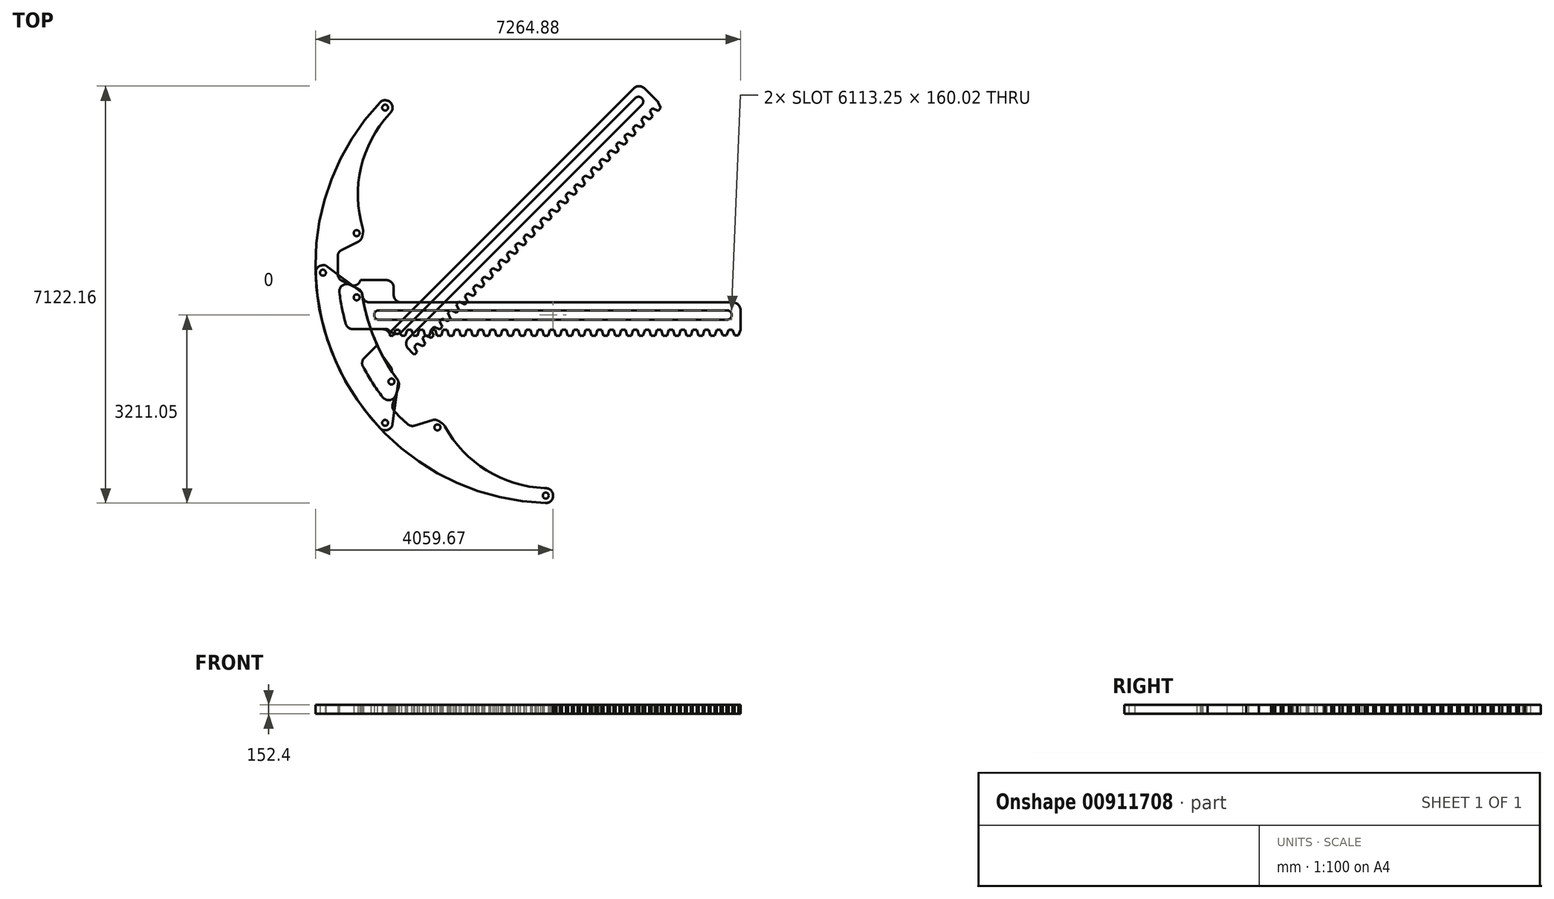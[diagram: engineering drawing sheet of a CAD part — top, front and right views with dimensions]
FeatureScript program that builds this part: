
annotation { "Feature Type Name" : "Feature", "Feature Type Description" : "" }
export const myFeature = defineFeature(function(context is Context, id is Id, definition is map)
    precondition{}
    {
        {
            var Q0;
            Q0=qCreatedBy(makeId("Top.planeOp"),FACE);
            var sketch = newSketch(context, id + "F0", { "sketchPlane" : qUnion([Q0])});
            skPoint(sketch, "E0.middle", {"position": v(0, 0) * mm});
            skCircle(sketch, "E1", {"center": v(0, 0) * mm, "radius": 3302 * mm});
            skCircle(sketch, "E2", {"center": v(0, 0) * mm, "radius": 3810 * mm});
            skCircle(sketch, "E3", {"center": v(0, 0) * mm, "radius": 3492.5 * mm, "construction": true});
            skCircle(sketch, "E4", {"center": v(0, 0) * mm, "radius": 4064 * mm});
            skLineSegment(sketch, "E5", {"start": v(0, 0) * mm, "end": v(-4064, 0) * mm});
            skCircle(sketch, "E6", {"center": v(0, 0) * mm, "radius": 3683 * mm});
            skLineSegment(sketch, "E7", {"start": v(-2740.49, -1842) * mm, "end": v(-3338.4, -1836.09) * mm});
            skLineSegment(sketch, "E8", {"start": v(-2604.27, -2604.27) * mm, "end": v(-2765.92, -2442.63) * mm});
            skLineSegment(sketch, "E9", {"start": v(-2765.92, -2442.63) * mm, "end": v(-2620.35, -2009.22) * mm});
            skLineSegment(sketch, "E10", {"start": v(0, 0) * mm, "end": v(-2873.68, -2873.68) * mm});
            skLineSegment(sketch, "E11.0", {"start": v(-2620.35, -2009.22) * mm, "end": v(-2596.8, -1985.68) * mm, "construction": true});
            skLineSegment(sketch, "E11.1", {"start": v(-2596.8, -1985.68) * mm, "end": v(-2740.49, -1842) * mm, "construction": true});
            skLineSegment(sketch, "E12", {"start": v(-2604.27, -2604.27) * mm, "end": v(-2437.7, -2760.82) * mm});
            skLineSegment(sketch, "E13", {"start": v(-2437.7, -2760.82) * mm, "end": v(-2000.51, -2627) * mm});
            skLineSegment(sketch, "E14", {"start": v(-2000.51, -2627) * mm, "end": v(-1835.14, -2745.08) * mm});
            skLineSegment(sketch, "E15", {"start": v(-1835.14, -2745.08) * mm, "end": v(-1845.2, -3333.36) * mm});
            skLineSegment(sketch, "E16", {"start": v(0, 0) * mm, "end": v(0, -4064) * mm});
            skCircle(sketch, "E17", {"center": v(-2763.42, -1986.96) * mm, "radius": 50.8 * mm});
            skCircle(sketch, "E18", {"center": v(-1977.77, -2770) * mm, "radius": 50.8 * mm});
            skLineSegment(sketch, "E19", {"start": v(0, 0) * mm, "end": v(-3299.6, -2372.49) * mm, "construction": true});
            skLineSegment(sketch, "E20", {"start": v(0, 0) * mm, "end": v(-2361.52, -3307.46) * mm, "construction": true});
            skCircle(sketch, "E21", {"center": v(-127, -3934.95) * mm, "radius": 50.8 * mm});
            skCircle(sketch, "E22", {"center": v(-3934.95, -127) * mm, "radius": 50.8 * mm});
            skSolve(sketch);
        }
        {
            var Q0;
            {var subQ0=sQuery(id+"F0.wireOp",EDGE,"E2");var subQ8=makeQuery(id+"F0.imprint","INTERSECT",VERTEX,{"derivedFrom":[subQ0,sQuery(id+"F0.wireOp",EDGE,"E7")]});Q0=makeQuery(id+"F0.imprint","IMPRINT",FACE,{"disambiguationData":[TD([[makeQuery(id+"F0.imprint","IMPRINT",EDGE,{"disambiguationData":[TD([[subQ8,1.0]])],"derivedFrom":subQ0}),-1.0]])]});}
            var Q1;
            {var subQ3=sQuery(id+"F0.wireOp",EDGE,"E7");Q1=makeQuery(id+"F0.imprint","IMPRINT",FACE,{"disambiguationData":[TD([[makeQuery(id+"F0.imprint","IMPRINT",EDGE,{"derivedFrom":subQ3}),1.0]])]});}
            var Q2;
            {var subQ0=sQuery(id+"F0.wireOp",EDGE,"E7");var subQ1=sQuery(id+"F0.wireOp",EDGE,"E1");var subQ2=makeQuery(id+"F0.imprint","INTERSECT",VERTEX,{"derivedFrom":[subQ1,subQ0]});Q2=makeQuery(id+"F0.imprint","IMPRINT",FACE,{"disambiguationData":[TD([[makeQuery(id+"F0.imprint","IMPRINT",EDGE,{"disambiguationData":[TD([[subQ2,-1.0]])],"derivedFrom":subQ1}),-1.0]])]});}
            var Q3;
            {var subQ0=sQuery(id+"F0.wireOp",EDGE,"E9");var subQ1=sQuery(id+"F0.wireOp",EDGE,"S5sV3fft-Mi81-JVDm-EhU3-nDH7DOH9WXkB");var subQ2=makeQuery(id+"F0.imprint","INTERSECT",VERTEX,{"derivedFrom":[subQ1,subQ0]});Q3=makeQuery(id+"F0.imprint","IMPRINT",FACE,{"disambiguationData":[TD([[makeQuery(id+"F0.imprint","IMPRINT",EDGE,{"disambiguationData":[TD([[subQ2,-1.0]])],"derivedFrom":subQ1}),1.0]])]});}
            var Q4;
            {var subQ9=sQuery(id+"F0.wireOp",EDGE,"E8");Q4=makeQuery(id+"F0.imprint","IMPRINT",FACE,{"disambiguationData":[TD([[makeQuery(id+"F0.imprint","IMPRINT",EDGE,{"derivedFrom":subQ9}),1.0]])]});}
            var Q5;
            {var subQ5=sQuery(id+"F0.wireOp",EDGE,"E2");var subQ6=makeQuery(id+"F0.imprint","INTERSECT",VERTEX,{"derivedFrom":[subQ5,sQuery(id+"F0.wireOp",EDGE,"E15")]});Q5=makeQuery(id+"F0.imprint","IMPRINT",FACE,{"disambiguationData":[TD([[makeQuery(id+"F0.imprint","IMPRINT",EDGE,{"disambiguationData":[TD([[subQ6,1.0]])],"derivedFrom":subQ5}),-1.0]])]});}
            var Q6;
            {var subQ4=sQuery(id+"F0.wireOp",EDGE,"E2");var subQ7=sQuery(id+"F0.wireOp",EDGE,"E15");var subQ9=makeQuery(id+"F0.imprint","INTERSECT",VERTEX,{"derivedFrom":[subQ4,subQ7]});Q6=makeQuery(id+"F0.imprint","IMPRINT",FACE,{"disambiguationData":[TD([[makeQuery(id+"F0.imprint","IMPRINT",EDGE,{"disambiguationData":[TD([[subQ9,1.0]])],"derivedFrom":subQ4}),1.0]])]});}
            var Q7;
            {var subQ1=sQuery(id+"F0.wireOp",EDGE,"E13");Q7=makeQuery(id+"F0.imprint","IMPRINT",FACE,{"disambiguationData":[TD([[makeQuery(id+"F0.imprint","IMPRINT",EDGE,{"derivedFrom":subQ1}),-1.0]])]});}
            var Q8;
            {var subQ0=sQuery(id+"F0.wireOp",EDGE,"E7");var subQ1=sQuery(id+"F0.wireOp",EDGE,"E1");var subQ2=makeQuery(id+"F0.imprint","INTERSECT",VERTEX,{"derivedFrom":[subQ1,subQ0]});Q8=makeQuery(id+"F0.imprint","IMPRINT",FACE,{"disambiguationData":[TD([[makeQuery(id+"F0.imprint","IMPRINT",EDGE,{"disambiguationData":[TD([[subQ2,1.0]])],"derivedFrom":subQ1}),-1.0]])]});}
            var Q9;
            {var subQ0=sQuery(id+"F0.wireOp",EDGE,"E7");var subQ1=sQuery(id+"F0.wireOp",EDGE,"E2");var subQ2=makeQuery(id+"F0.imprint","INTERSECT",VERTEX,{"derivedFrom":[subQ1,subQ0]});Q9=makeQuery(id+"F0.imprint","IMPRINT",FACE,{"disambiguationData":[TD([[makeQuery(id+"F0.imprint","IMPRINT",EDGE,{"disambiguationData":[TD([[subQ2,1.0]])],"derivedFrom":subQ1}),1.0]])]});}
            extrude(context, id + "F1", {"entities" : qUnion([Q0, Q1, Q2, Q3, Q4, Q5, Q6, Q7, Q8, Q9]), "depth" : 152.4 * mm, "offsetDistance" : 25.4 * mm});
        }
        {
            var Q0;
            Q0=makeQuery(id+"F1.opExtrude","SWEPT_EDGE",EDGE,{"disambiguationData":[OSD([sQuery(id+"F0.wireOp",EDGE,"E4"),sQuery(id+"F0.wireOp",EDGE,"E5")])]});
            var Q1;
            Q1=makeQuery(id+"F1.opExtrude","SWEPT_EDGE",EDGE,{"disambiguationData":[OSD([sQuery(id+"F0.wireOp",EDGE,"E2"),sQuery(id+"F0.wireOp",EDGE,"E16")])]});
            var Q2;
            Q2=makeQuery(id+"F1.opExtrude","SWEPT_EDGE",EDGE,{"disambiguationData":[OSD([sQuery(id+"F0.wireOp",EDGE,"E1"),sQuery(id+"F0.wireOp",EDGE,"E9")])]});
            var Q3;
            Q3=makeQuery(id+"F1.opExtrude","SWEPT_EDGE",EDGE,{"disambiguationData":[OSD([sQuery(id+"F0.wireOp",EDGE,"E8"),sQuery(id+"F0.wireOp",EDGE,"E9")])]});
            var Q4;
            Q4=makeQuery(id+"F1.opExtrude","SWEPT_EDGE",EDGE,{"disambiguationData":[OSD([sQuery(id+"F0.wireOp",EDGE,"E4"),sQuery(id+"F0.wireOp",EDGE,"E16")])]});
            var Q5;
            Q5=makeQuery(id+"F1.opExtrude","SWEPT_EDGE",EDGE,{"disambiguationData":[OSD([sQuery(id+"F0.wireOp",EDGE,"E6"),sQuery(id+"F0.wireOp",EDGE,"E12"),sQuery(id+"F0.wireOp",EDGE,"E13")])]});
            var Q6;
            Q6=makeQuery(id+"F1.opExtrude","SWEPT_EDGE",EDGE,{"disambiguationData":[OSD([sQuery(id+"F0.wireOp",EDGE,"E1"),sQuery(id+"F0.wireOp",EDGE,"E13"),sQuery(id+"F0.wireOp",EDGE,"E14")])]});
            var Q7;
            Q7=makeQuery(id+"F1.opExtrude","SWEPT_EDGE",EDGE,{"disambiguationData":[OSD([sQuery(id+"F0.wireOp",EDGE,"E1"),sQuery(id+"F0.wireOp",EDGE,"E14"),sQuery(id+"F0.wireOp",EDGE,"E15")])]});
            fillet(context, id + "F2", {"entities" : qUnion([Q0, Q1, Q2, Q3, Q4, Q5, Q6, Q7]), "tangentPropagation" : true, "radius" : 127 * mm, "defaultsChanged" : false, "vertexSettings" : [], "allowEdgeOverflow" : false});
        }
        {
            var Q0;
            Q0=makeQuery(id+"F1.opExtrude","SWEPT_EDGE",EDGE,{"disambiguationData":[OSD([sQuery(id+"F0.wireOp",EDGE,"E2"),sQuery(id+"F0.wireOp",EDGE,"E7")])]});
            fillet(context, id + "F3", {"entities" : qUnion([Q0]), "tangentPropagation" : true, "radius" : 2032 * mm, "defaultsChanged" : true, "vertexSettings" : [], "allowEdgeOverflow" : false});
        }
        {
            var Q0;
            Q0=makeQuery(id+"F1.opExtrude","SWEPT_EDGE",EDGE,{"disambiguationData":[OSD([sQuery(id+"F0.wireOp",EDGE,"E1"),sQuery(id+"F0.wireOp",EDGE,"E5")])]});
            chamfer(context, id + "F4", {"entities" : qUnion([Q0]), "chamferType" : ChamferType.TWO_OFFSETS, "width1" : 635 * mm, "oppositeDirection" : false, "width2" : 558.8 * mm, "tangentPropagation" : true});
        }
        {
            var Q0;
            Q0=qCreatedBy(makeId("Top.planeOp"),FACE);
            var sketch = newSketch(context, id + "F5", { "sketchPlane" : qUnion([Q0])});
            skLineSegment(sketch, "E23.bottom", {"start": v(-1246.87, 397.58) * mm, "end": v(-348.84, 1295.6) * mm, "construction": true});
            skLineSegment(sketch, "E23.top", {"start": v(-635, 635) * mm, "end": v(635, 635) * mm, "construction": true});
            skLineSegment(sketch, "E23.left", {"start": v(-635, -635) * mm, "end": v(-635, 635) * mm, "construction": true});
            skLineSegment(sketch, "E23.right", {"start": v(635, -635) * mm, "end": v(635, 635) * mm, "construction": true});
            skPoint(sketch, "E23.middle", {"position": v(0, 0) * mm});
            skPoint(sketch, "E24", {"position": v(-797.85, 846.59) * mm});
            skLineSegment(sketch, "E25", {"start": v(1361.64, 2205.6) * mm, "end": v(1407.84, 2251.8) * mm});
            skLineSegment(sketch, "E26", {"start": v(1407.84, 2251.8) * mm, "end": v(1363.07, 2347.79) * mm});
            skLineSegment(sketch, "E27", {"start": v(1217.98, 2061.94) * mm, "end": v(1263.67, 2107.62) * mm});
            skLineSegment(sketch, "E28", {"start": v(1263.67, 2107.62) * mm, "end": v(1218.9, 2203.61) * mm});
            skLineSegment(sketch, "E29", {"start": v(1218.9, 2203.61) * mm, "end": v(1265.64, 2250.36) * mm});
            skLineSegment(sketch, "E30", {"start": v(1265.64, 2250.36) * mm, "end": v(1361.64, 2205.6) * mm});
            skLineSegment(sketch, "E31", {"start": v(1074.32, 1918.28) * mm, "end": v(1120, 1963.96) * mm});
            skLineSegment(sketch, "E32", {"start": v(1120, 1963.96) * mm, "end": v(1075.25, 2059.96) * mm});
            skLineSegment(sketch, "E33", {"start": v(1075.25, 2059.96) * mm, "end": v(1121.99, 2106.7) * mm});
            skLineSegment(sketch, "E34", {"start": v(1121.99, 2106.7) * mm, "end": v(1217.98, 2061.94) * mm});
            skLineSegment(sketch, "E35", {"start": v(930.67, 1774.62) * mm, "end": v(976.35, 1820.3) * mm});
            skLineSegment(sketch, "E36", {"start": v(976.35, 1820.3) * mm, "end": v(931.59, 1916.3) * mm});
            skLineSegment(sketch, "E37", {"start": v(931.59, 1916.3) * mm, "end": v(978.33, 1963.04) * mm});
            skLineSegment(sketch, "E38", {"start": v(978.33, 1963.04) * mm, "end": v(1074.32, 1918.28) * mm});
            skLineSegment(sketch, "E39", {"start": v(787, 1630.97) * mm, "end": v(832.7, 1676.65) * mm});
            skLineSegment(sketch, "E40", {"start": v(832.7, 1676.65) * mm, "end": v(787.93, 1772.64) * mm});
            skLineSegment(sketch, "E41", {"start": v(787.93, 1772.64) * mm, "end": v(834.67, 1819.38) * mm});
            skLineSegment(sketch, "E42", {"start": v(834.67, 1819.38) * mm, "end": v(930.67, 1774.62) * mm});
            skLineSegment(sketch, "E43", {"start": v(643.35, 1487.3) * mm, "end": v(689.04, 1533) * mm});
            skLineSegment(sketch, "E44", {"start": v(689.04, 1533) * mm, "end": v(644.27, 1628.99) * mm});
            skLineSegment(sketch, "E45", {"start": v(644.27, 1628.99) * mm, "end": v(691.02, 1675.73) * mm});
            skLineSegment(sketch, "E46", {"start": v(691.02, 1675.73) * mm, "end": v(787, 1630.97) * mm});
            skLineSegment(sketch, "E47", {"start": v(499.7, 1343.65) * mm, "end": v(545.38, 1389.34) * mm});
            skLineSegment(sketch, "E48", {"start": v(545.38, 1389.34) * mm, "end": v(500.62, 1485.33) * mm});
            skLineSegment(sketch, "E49", {"start": v(500.62, 1485.33) * mm, "end": v(547.36, 1532.07) * mm});
            skLineSegment(sketch, "E50", {"start": v(547.36, 1532.07) * mm, "end": v(643.35, 1487.3) * mm});
            skLineSegment(sketch, "E51", {"start": v(356.04, 1200) * mm, "end": v(401.72, 1245.68) * mm});
            skLineSegment(sketch, "E52", {"start": v(401.72, 1245.68) * mm, "end": v(356.96, 1341.67) * mm});
            skLineSegment(sketch, "E53", {"start": v(356.96, 1341.67) * mm, "end": v(403.7, 1388.41) * mm});
            skLineSegment(sketch, "E54", {"start": v(403.7, 1388.41) * mm, "end": v(499.7, 1343.65) * mm});
            skLineSegment(sketch, "E55", {"start": v(212.38, 1056.34) * mm, "end": v(258.07, 1102.02) * mm});
            skLineSegment(sketch, "E56", {"start": v(258.07, 1102.02) * mm, "end": v(213.3, 1198.02) * mm});
            skLineSegment(sketch, "E57", {"start": v(213.3, 1198.02) * mm, "end": v(260.04, 1244.76) * mm});
            skLineSegment(sketch, "E58", {"start": v(260.04, 1244.76) * mm, "end": v(356.04, 1200) * mm});
            skLineSegment(sketch, "E59", {"start": v(68.72, 912.68) * mm, "end": v(114.4, 958.37) * mm});
            skLineSegment(sketch, "E60", {"start": v(114.4, 958.37) * mm, "end": v(69.65, 1054.36) * mm});
            skLineSegment(sketch, "E61", {"start": v(69.65, 1054.36) * mm, "end": v(116.39, 1101.1) * mm});
            skLineSegment(sketch, "E62", {"start": v(116.39, 1101.1) * mm, "end": v(212.38, 1056.34) * mm});
            skLineSegment(sketch, "E63", {"start": v(-74.93, 769.02) * mm, "end": v(-29.25, 814.7) * mm});
            skLineSegment(sketch, "E64", {"start": v(-29.25, 814.7) * mm, "end": v(-74.01, 910.7) * mm});
            skLineSegment(sketch, "E65", {"start": v(-74.01, 910.7) * mm, "end": v(-27.27, 957.44) * mm});
            skLineSegment(sketch, "E66", {"start": v(-27.27, 957.44) * mm, "end": v(68.72, 912.68) * mm});
            skLineSegment(sketch, "E67", {"start": v(-218.6, 625.37) * mm, "end": v(-172.9, 671.05) * mm});
            skLineSegment(sketch, "E68", {"start": v(-172.9, 671.05) * mm, "end": v(-217.67, 767.04) * mm});
            skLineSegment(sketch, "E69", {"start": v(-217.67, 767.04) * mm, "end": v(-170.93, 813.79) * mm});
            skLineSegment(sketch, "E70", {"start": v(-170.93, 813.79) * mm, "end": v(-74.93, 769.02) * mm});
            skLineSegment(sketch, "E71", {"start": v(-362.25, 481.7) * mm, "end": v(-316.56, 527.4) * mm});
            skLineSegment(sketch, "E72", {"start": v(-316.56, 527.4) * mm, "end": v(-361.33, 623.39) * mm});
            skLineSegment(sketch, "E73", {"start": v(-361.33, 623.39) * mm, "end": v(-314.58, 670.13) * mm});
            skLineSegment(sketch, "E74", {"start": v(-314.58, 670.13) * mm, "end": v(-218.6, 625.37) * mm});
            skLineSegment(sketch, "E75", {"start": v(-505.9, 338.05) * mm, "end": v(-460.22, 383.74) * mm});
            skLineSegment(sketch, "E76", {"start": v(-460.22, 383.74) * mm, "end": v(-504.98, 479.73) * mm});
            skLineSegment(sketch, "E77", {"start": v(-504.98, 479.73) * mm, "end": v(-458.24, 526.47) * mm});
            skLineSegment(sketch, "E78", {"start": v(-458.24, 526.47) * mm, "end": v(-362.25, 481.7) * mm});
            skLineSegment(sketch, "E79", {"start": v(-649.56, 194.4) * mm, "end": v(-603.88, 240.08) * mm});
            skLineSegment(sketch, "E80", {"start": v(-603.88, 240.08) * mm, "end": v(-648.64, 336.07) * mm});
            skLineSegment(sketch, "E81", {"start": v(-648.64, 336.07) * mm, "end": v(-601.9, 382.81) * mm});
            skLineSegment(sketch, "E82", {"start": v(-601.9, 382.81) * mm, "end": v(-505.9, 338.05) * mm});
            skLineSegment(sketch, "E83", {"start": v(-793.22, 50.74) * mm, "end": v(-747.53, 96.42) * mm});
            skLineSegment(sketch, "E84", {"start": v(-747.53, 96.42) * mm, "end": v(-792.3, 192.42) * mm});
            skLineSegment(sketch, "E85", {"start": v(-792.3, 192.42) * mm, "end": v(-745.55, 239.16) * mm});
            skLineSegment(sketch, "E86", {"start": v(-745.55, 239.16) * mm, "end": v(-649.56, 194.4) * mm});
            skLineSegment(sketch, "E87", {"start": v(-936.88, -92.92) * mm, "end": v(-891.2, -47.23) * mm});
            skLineSegment(sketch, "E88", {"start": v(-891.2, -47.23) * mm, "end": v(-935.95, 48.76) * mm});
            skLineSegment(sketch, "E89", {"start": v(-935.95, 48.76) * mm, "end": v(-889.21, 95.5) * mm});
            skLineSegment(sketch, "E90", {"start": v(-889.21, 95.5) * mm, "end": v(-793.22, 50.74) * mm});
            skLineSegment(sketch, "E91", {"start": v(-1080.53, -236.58) * mm, "end": v(-1034.85, -190.9) * mm});
            skLineSegment(sketch, "E92", {"start": v(-1034.85, -190.9) * mm, "end": v(-1079.61, -94.9) * mm});
            skLineSegment(sketch, "E93", {"start": v(-1079.61, -94.9) * mm, "end": v(-1032.87, -48.16) * mm});
            skLineSegment(sketch, "E94", {"start": v(-1032.87, -48.16) * mm, "end": v(-936.88, -92.92) * mm});
            skLineSegment(sketch, "E95", {"start": v(-1224.2, -380.23) * mm, "end": v(-1178.5, -334.55) * mm});
            skLineSegment(sketch, "E96", {"start": v(-1178.5, -334.55) * mm, "end": v(-1223.27, -238.56) * mm});
            skLineSegment(sketch, "E97", {"start": v(-1223.27, -238.56) * mm, "end": v(-1176.53, -191.81) * mm});
            skLineSegment(sketch, "E98", {"start": v(-1176.53, -191.81) * mm, "end": v(-1080.53, -236.58) * mm});
            skLineSegment(sketch, "E99", {"start": v(-1367.85, -523.9) * mm, "end": v(-1322.16, -478.2) * mm});
            skLineSegment(sketch, "E100", {"start": v(-1322.16, -478.2) * mm, "end": v(-1366.92, -382.21) * mm});
            skLineSegment(sketch, "E101", {"start": v(-1366.92, -382.21) * mm, "end": v(-1320.18, -335.47) * mm});
            skLineSegment(sketch, "E102", {"start": v(-1320.18, -335.47) * mm, "end": v(-1224.2, -380.23) * mm});
            skLineSegment(sketch, "E103", {"start": v(-1511.5, -667.55) * mm, "end": v(-1465.82, -621.86) * mm});
            skLineSegment(sketch, "E104", {"start": v(-1465.82, -621.86) * mm, "end": v(-1510.58, -525.87) * mm});
            skLineSegment(sketch, "E105", {"start": v(-1510.58, -525.87) * mm, "end": v(-1463.84, -479.13) * mm});
            skLineSegment(sketch, "E106", {"start": v(-1463.84, -479.13) * mm, "end": v(-1367.85, -523.9) * mm});
            skLineSegment(sketch, "E107", {"start": v(-1655.16, -811.2) * mm, "end": v(-1609.48, -765.52) * mm});
            skLineSegment(sketch, "E108", {"start": v(-1609.48, -765.52) * mm, "end": v(-1654.24, -669.53) * mm});
            skLineSegment(sketch, "E109", {"start": v(-1654.24, -669.53) * mm, "end": v(-1607.5, -622.79) * mm});
            skLineSegment(sketch, "E110", {"start": v(-1607.5, -622.79) * mm, "end": v(-1511.5, -667.55) * mm});
            skLineSegment(sketch, "E111", {"start": v(-1798.82, -954.86) * mm, "end": v(-1753.13, -909.18) * mm});
            skLineSegment(sketch, "E112", {"start": v(-1753.13, -909.18) * mm, "end": v(-1797.9, -813.18) * mm});
            skLineSegment(sketch, "E113", {"start": v(-1797.9, -813.18) * mm, "end": v(-1751.15, -766.44) * mm});
            skLineSegment(sketch, "E114", {"start": v(-1751.15, -766.44) * mm, "end": v(-1655.16, -811.2) * mm});
            skLineSegment(sketch, "E115", {"start": v(-1942.48, -1098.52) * mm, "end": v(-1896.8, -1052.83) * mm});
            skLineSegment(sketch, "E116", {"start": v(-1896.8, -1052.83) * mm, "end": v(-1941.55, -956.84) * mm});
            skLineSegment(sketch, "E117", {"start": v(-1941.55, -956.84) * mm, "end": v(-1894.81, -910.1) * mm});
            skLineSegment(sketch, "E118", {"start": v(-1894.81, -910.1) * mm, "end": v(-1798.82, -954.86) * mm});
            skLineSegment(sketch, "E119", {"start": v(-2086.3, -1242.34) * mm, "end": v(-2040.45, -1196.5) * mm});
            skLineSegment(sketch, "E120", {"start": v(-2040.45, -1196.5) * mm, "end": v(-2085.2, -1100.5) * mm});
            skLineSegment(sketch, "E121", {"start": v(-2085.2, -1100.5) * mm, "end": v(-2038.47, -1053.76) * mm});
            skLineSegment(sketch, "E122", {"start": v(-2038.47, -1053.76) * mm, "end": v(-1942.48, -1098.52) * mm});
            skLineSegment(sketch, "E123", {"start": v(-2229.69, -1244.98) * mm, "end": v(-2182.29, -1197.58) * mm});
            skLineSegment(sketch, "E124", {"start": v(-2182.29, -1197.58) * mm, "end": v(-2086.3, -1242.34) * mm});
            skCircle(sketch, "E125", {"center": v(-3038.04, -1698.93) * mm, "radius": 50.8 * mm});
            skLineSegment(sketch, "E126", {"start": v(-2228.74, -1384.84) * mm, "end": v(-2184.93, -1340.97) * mm});
            skLineSegment(sketch, "E127", {"start": v(-2184.93, -1340.97) * mm, "end": v(-2229.69, -1244.98) * mm});
            skLineSegment(sketch, "E128", {"start": v(1505.8, 2349.76) * mm, "end": v(1552, 2395.96) * mm});
            skLineSegment(sketch, "E129", {"start": v(1552, 2395.96) * mm, "end": v(1507.6, 2492.51) * mm});
            skLineSegment(sketch, "E130", {"start": v(1363.07, 2347.79) * mm, "end": v(1409.81, 2394.53) * mm});
            skLineSegment(sketch, "E131", {"start": v(1409.81, 2394.53) * mm, "end": v(1505.8, 2349.76) * mm});
            skCircle(sketch, "E132", {"center": v(-2753, -1413.9) * mm, "radius": 80.01 * mm});
            skCircle(sketch, "E133", {"center": v(1459.4, 2798.5) * mm, "radius": 80.01 * mm});
            skLineSegment(sketch, "E134", {"start": v(-2809.58, -1357.32) * mm, "end": v(1402.82, 2855.08) * mm});
            skLineSegment(sketch, "E135", {"start": v(1515.97, 2741.93) * mm, "end": v(-2696.43, -1470.47) * mm});
            skLineSegment(sketch, "E136.bottom", {"start": v(-2773.5, -1129.07) * mm, "end": v(1177.8, 2822.25) * mm});
            skLineSegment(sketch, "E136.top", {"start": v(-2408.5, -1494.07) * mm, "end": v(1833.38, 2747.81) * mm, "construction": true});
            skLineSegment(sketch, "E136.left", {"start": v(-2773.5, -1129.07) * mm, "end": v(-2408.5, -1494.07) * mm});
            skLineSegment(sketch, "E137", {"start": v(-2373.22, -1529.33) * mm, "end": v(-2408.5, -1494.07) * mm});
            skLineSegment(sketch, "E138.bottom", {"start": v(-2773.5, -1129.07) * mm, "end": v(-3354.68, -1710.24) * mm});
            skLineSegment(sketch, "E138.top", {"start": v(-2450.22, -1452.36) * mm, "end": v(-3031.4, -2033.53) * mm});
            skLineSegment(sketch, "E138.left", {"start": v(-2773.5, -1129.07) * mm, "end": v(-2450.22, -1452.36) * mm});
            skLineSegment(sketch, "E138.right", {"start": v(-3354.68, -1710.24) * mm, "end": v(-3031.4, -2033.53) * mm});
            skLineSegment(sketch, "E139.bottom", {"start": v(1177.8, 2822.25) * mm, "end": v(1468.37, 3112.82) * mm});
            skLineSegment(sketch, "E139.right", {"start": v(1468.37, 3112.82) * mm, "end": v(1891.82, 2689.37) * mm});
            skPoint(sketch, "E140", {"position": v(1147.13, 2791.58) * mm});
            skLineSegment(sketch, "E141", {"start": v(1650.33, 2494.5) * mm, "end": v(1696.53, 2540.7) * mm});
            skLineSegment(sketch, "E142", {"start": v(1696.53, 2540.7) * mm, "end": v(1652.11, 2637.24) * mm});
            skLineSegment(sketch, "E143", {"start": v(1507.6, 2492.51) * mm, "end": v(1554.34, 2539.25) * mm});
            skLineSegment(sketch, "E144", {"start": v(1554.34, 2539.25) * mm, "end": v(1650.33, 2494.5) * mm});
            skLineSegment(sketch, "E145", {"start": v(1794.85, 2639.22) * mm, "end": v(1841.05, 2685.42) * mm});
            skLineSegment(sketch, "E146", {"start": v(1841.05, 2685.42) * mm, "end": v(1796.64, 2781.97) * mm});
            skLineSegment(sketch, "E147", {"start": v(1652.11, 2637.24) * mm, "end": v(1698.86, 2683.98) * mm});
            skLineSegment(sketch, "E148", {"start": v(1698.86, 2683.98) * mm, "end": v(1794.85, 2639.22) * mm});
            skPoint(sketch, "E149", {"position": v(1833.38, 2747.81) * mm});
            skPoint(sketch, "E149.positionSnap0", {"position": v(2108.14, 3022.58) * mm});
            skLineSegment(sketch, "E150.bottom", {"start": v(-2995.47, -1351.03) * mm, "end": v(-2815.87, -1171.43) * mm});
            skPoint(sketch, "E151", {"position": v(-2905.67, -1261.23) * mm});
            skCircle(sketch, "E152", {"center": v(0, 0) * mm, "radius": 3302 * mm});
            skCircle(sketch, "E153", {"center": v(0, 0) * mm, "radius": 3683 * mm});
            skCircle(sketch, "E154", {"center": v(0, 0) * mm, "radius": 3492.5 * mm, "construction": true});
            skLineSegment(sketch, "E155", {"start": v(-2753, -1413.9) * mm, "end": v(-3202.02, -1862.9) * mm, "construction": true});
            skLineSegment(sketch, "E156", {"start": v(0, 0) * mm, "end": v(-3683, 0) * mm, "construction": true});
            skCircle(sketch, "E157", {"center": v(-3492.5, 0) * mm, "radius": 50.8 * mm});
            skLineSegment(sketch, "E158", {"start": v(0, 0) * mm, "end": v(-3674.03, 256.91) * mm});
            skCircle(sketch, "E159", {"center": v(-2202.71, -863.6) * mm, "radius": 80.01 * mm});
            skLineSegment(sketch, "E160.0", {"start": v(1147.13, 2791.58) * mm, "end": v(1468.37, 3112.82) * mm, "construction": true});
            skLineSegment(sketch, "E160.1", {"start": v(1147.13, 2791.58) * mm, "end": v(1147.13, 2791.58) * mm});
            skLineSegment(sketch, "E160.8", {"start": v(-2373.24, -1529.34) * mm, "end": v(-2373.22, -1529.33) * mm, "construction": true});
            skLineSegment(sketch, "E160.9", {"start": v(-2373.24, -1529.34) * mm, "end": v(-2773.5, -1129.07) * mm, "construction": true});
            skLineSegment(sketch, "E160.16", {"start": v(-2753, -1413.9) * mm, "end": v(-2202.71, -863.6) * mm, "construction": true});
            skLineSegment(sketch, "E160.17", {"start": v(-2753, -1413.9) * mm, "end": v(-2753, -1413.9) * mm});
            skLineSegment(sketch, "E161.0", {"start": v(-3038.04, -1698.93) * mm, "end": v(-2202.71, -863.6) * mm, "construction": true});
            skLineSegment(sketch, "E162.0", {"start": v(1833.38, 2747.81) * mm, "end": v(2108.14, 3022.58) * mm, "construction": true});
            skLineSegment(sketch, "E163.0", {"start": v(-2373.22, -1529.33) * mm, "end": v(-2228.74, -1384.84) * mm, "construction": true});
            skLineSegment(sketch, "E164.0", {"start": v(-2696.43, -1470.47) * mm, "end": v(-2905.67, -1261.23) * mm, "construction": true});
            skLineSegment(sketch, "E165.0", {"start": v(1515.97, 2741.93) * mm, "end": v(1402.82, 2855.08) * mm, "construction": true});
            skLineSegment(sketch, "E166.0", {"start": v(1796.64, 2781.97) * mm, "end": v(1796.64, 2781.97) * mm});
            skLineSegment(sketch, "E167", {"start": v(0, 0) * mm, "end": v(-2604.27, -2604.27) * mm, "construction": true});
            skLineSegment(sketch, "E168", {"start": v(-635, -635) * mm, "end": v(635, -635) * mm, "construction": true});
            skCircle(sketch, "E169", {"center": v(-2469.57, -2469.57) * mm, "radius": 50.8 * mm});
            skLineSegment(sketch, "E170", {"start": v(0, 0) * mm, "end": v(-2416.27, -2779.6) * mm});
            skLineSegment(sketch, "E171", {"start": v(-3214.51, -1797.61) * mm, "end": v(0, 0) * mm, "construction": true});
            skCircle(sketch, "E172", {"center": v(0, 0) * mm, "radius": 4064 * mm});
            skLineSegment(sketch, "E173", {"start": v(0, 0) * mm, "end": v(-4064, 0) * mm, "construction": true});
            skLineSegment(sketch, "E174", {"start": v(-3683, 0) * mm, "end": v(-4064, 0) * mm});
            skCircle(sketch, "E175", {"center": v(0, 0) * mm, "radius": 3810 * mm});
            skLineSegment(sketch, "E176", {"start": v(-3293.3, -1648.85) * mm, "end": v(-3354.68, -1710.24) * mm});
            skLineSegment(sketch, "E177", {"start": v(0, 0) * mm, "end": v(-3034.19, -2304.3) * mm});
            skLineSegment(sketch, "E178", {"start": v(-2505.5, -2505.5) * mm, "end": v(-2873.68, -2873.68) * mm});
            skLineSegment(sketch, "E179", {"start": v(-2433.65, -2433.65) * mm, "end": v(-2334.87, -2334.87) * mm});
            skLineSegment(sketch, "E180", {"start": v(-4064, 0) * mm, "end": v(-2334.87, -2334.87) * mm});
            skPoint(sketch, "E181", {"position": v(-2604.27, -2604.27) * mm});
            skLineSegment(sketch, "E182", {"start": v(-2505.5, -2505.5) * mm, "end": v(-2433.65, -2433.65) * mm});
            skLineSegment(sketch, "E183", {"start": v(-2372.2, -1387.48) * mm, "end": v(-2324.8, -1340.08) * mm});
            skLineSegment(sketch, "E184", {"start": v(-2324.8, -1340.08) * mm, "end": v(-2228.74, -1384.84) * mm});
            skLineSegment(sketch, "E185", {"start": v(-2373.24, -1529.34) * mm, "end": v(-2327.43, -1483.47) * mm});
            skLineSegment(sketch, "E186", {"start": v(-2327.43, -1483.47) * mm, "end": v(-2372.2, -1387.48) * mm});
            skLineSegment(sketch, "E187", {"start": v(1796.64, 2781.97) * mm, "end": v(1797.93, 2783.26) * mm});
            skLineSegment(sketch, "E188", {"start": v(-2604.27, -2604.27) * mm, "end": v(-2765.92, -2442.63) * mm});
            skLineSegment(sketch, "E189", {"start": v(-2765.92, -2442.63) * mm, "end": v(-2620.35, -2009.22) * mm});
            skLineSegment(sketch, "E190", {"start": v(-2753.09, -1823.1) * mm, "end": v(-3348.7, -1817.23) * mm});
            skSolve(sketch);
        }
        {
            var Q0;
            Q0=makeQuery(id+"F5.imprint","IMPRINT",FACE,{"disambiguationData":[TD([[makeQuery(id+"F5.imprint","IMPRINT",EDGE,{"derivedFrom":sQuery(id+"F5.wireOp",EDGE,"E25")}),1.0]])]});
            var Q1;
            {var subQ5=sQuery(id+"F5.wireOp",EDGE,"E187");Q1=makeQuery(id+"F5.imprint","IMPRINT",FACE,{"disambiguationData":[TD([[makeQuery(id+"F5.imprint","IMPRINT",EDGE,{"derivedFrom":subQ5}),1.0]])]});}
            var Q2;
            {var subQ0=sQuery(id+"F5.wireOp",EDGE,"E138.left");var subQ3=sQuery(id+"F5.wireOp",EDGE,"E134");var subQ4=makeQuery(id+"F5.imprint","INTERSECT",VERTEX,{"derivedFrom":[subQ3,subQ0]});Q2=makeQuery(id+"F5.imprint","IMPRINT",FACE,{"disambiguationData":[TD([[makeQuery(id+"F5.imprint","IMPRINT",EDGE,{"disambiguationData":[TD([[subQ4,-1.0]])],"derivedFrom":subQ3}),1.0]])]});}
            var Q3;
            Q3=makeQuery(id+"F5.imprint","IMPRINT",FACE,{"disambiguationData":[TD([[makeQuery(id+"F5.imprint","IMPRINT",EDGE,{"derivedFrom":sQuery(id+"F5.wireOp",EDGE,"E87")}),1.0]])]});
            var Q4;
            {var subQ0=sQuery(id+"F5.wireOp",EDGE,"E150.bottom");Q4=makeQuery(id+"F5.imprint","IMPRINT",FACE,{"disambiguationData":[TD([[makeQuery(id+"F5.imprint","IMPRINT",EDGE,{"derivedFrom":subQ0}),-1.0]])]});}
            var Q5;
            Q5=makeQuery(id+"F5.imprint","IMPRINT",FACE,{"disambiguationData":[TD([[makeQuery(id+"F5.imprint","IMPRINT",EDGE,{"derivedFrom":sQuery(id+"F5.wireOp",EDGE,"E125")}),-1.0]])]});
            var Q6;
            {var subQ0=sQuery(id+"F5.wireOp",EDGE,"E152");var subQ1=sQuery(id+"F5.wireOp",EDGE,"E138.bottom");var subQ2=makeQuery(id+"F5.imprint","INTERSECT",VERTEX,{"derivedFrom":[subQ1,subQ0]});Q6=makeQuery(id+"F5.imprint","IMPRINT",FACE,{"disambiguationData":[TD([[makeQuery(id+"F5.imprint","IMPRINT",EDGE,{"disambiguationData":[TD([[subQ2,-1.0]])],"derivedFrom":subQ1}),1.0]])]});}
            var Q7;
            {var subQ0=sQuery(id+"F5.wireOp",EDGE,"E180");var subQ1=sQuery(id+"F5.wireOp",EDGE,"E138.top");var subQ2=makeQuery(id+"F5.imprint","INTERSECT",VERTEX,{"derivedFrom":[subQ1,subQ0]});Q7=makeQuery(id+"F5.imprint","IMPRINT",FACE,{"disambiguationData":[TD([[makeQuery(id+"F5.imprint","IMPRINT",EDGE,{"disambiguationData":[TD([[subQ2,-1.0]])],"derivedFrom":subQ1}),-1.0]])]});}
            var Q8;
            {var subQ0=sQuery(id+"F5.wireOp",EDGE,"E138.right");var subQ1=sQuery(id+"F5.wireOp",EDGE,"E138.top");var subQ2=makeQuery(id+"F5.imprint","INTERSECT",VERTEX,{"derivedFrom":[subQ1,subQ0]});Q8=makeQuery(id+"F5.imprint","IMPRINT",FACE,{"disambiguationData":[TD([[makeQuery(id+"F5.imprint","IMPRINT",EDGE,{"disambiguationData":[TD([[subQ2,1.0]])],"derivedFrom":subQ1}),-1.0]])]});}
            var Q9;
            {var subQ1=sQuery(id+"F5.wireOp",EDGE,"E138.right");var subQ9=sQuery(id+"F5.wireOp",EDGE,"E138.top");var subQ10=makeQuery(id+"F5.imprint","INTERSECT",VERTEX,{"derivedFrom":[subQ9,subQ1]});Q9=makeQuery(id+"F5.imprint","IMPRINT",FACE,{"disambiguationData":[TD([[makeQuery(id+"F5.imprint","IMPRINT",EDGE,{"disambiguationData":[TD([[subQ10,1.0]])],"derivedFrom":subQ9}),1.0]])]});}
            var Q10;
            {var subQ0=sQuery(id+"F5.wireOp",EDGE,"E189");var subQ1=sQuery(id+"F5.wireOp",EDGE,"E152");var subQ2=makeQuery(id+"F5.imprint","INTERSECT",VERTEX,{"derivedFrom":[subQ1,subQ0]});Q10=makeQuery(id+"F5.imprint","IMPRINT",FACE,{"disambiguationData":[TD([[makeQuery(id+"F5.imprint","IMPRINT",EDGE,{"disambiguationData":[TD([[subQ2,1.0]])],"derivedFrom":subQ1}),-1.0]])]});}
            var Q11;
            {var subQ0=sQuery(id+"F5.wireOp",EDGE,"E152");var subQ1=sQuery(id+"F5.wireOp",EDGE,"E138.top");var subQ2=makeQuery(id+"F5.imprint","INTERSECT",VERTEX,{"derivedFrom":[subQ1,subQ0]});Q11=makeQuery(id+"F5.imprint","IMPRINT",FACE,{"disambiguationData":[TD([[makeQuery(id+"F5.imprint","IMPRINT",EDGE,{"disambiguationData":[TD([[subQ2,-1.0]])],"derivedFrom":subQ1}),1.0]])]});}
            var Q12;
            Q12=makeQuery(id+"F5.imprint","IMPRINT",FACE,{"disambiguationData":[TD([[makeQuery(id+"F5.imprint","IMPRINT",EDGE,{"derivedFrom":sQuery(id+"F5.wireOp",EDGE,"E125")}),1.0]])]});
            extrude(context, id + "F6", {"entities" : qUnion([Q0, Q1, Q2, Q3, Q4, Q5, Q6, Q7, Q8, Q9, Q10, Q11, Q12]), "depth" : 152.4 * mm, "offsetDistance" : 25.4 * mm});
        }
        {
            var Q0;
            Q0=makeQuery(id+"F6.opExtrude","SWEPT_EDGE",EDGE,{"disambiguationData":[OSD([sQuery(id+"F5.wireOp",EDGE,"E153"),sQuery(id+"F5.wireOp",EDGE,"E189")])]});
            var Q1;
            Q1=makeQuery(id+"F6.opExtrude","SWEPT_EDGE",EDGE,{"disambiguationData":[OSD([sQuery(id+"F5.wireOp",EDGE,"E152"),sQuery(id+"F5.wireOp",EDGE,"E189")])]});
            var Q2;
            Q2=makeQuery(id+"F6.opExtrude","SWEPT_EDGE",EDGE,{"disambiguationData":[OSD([sQuery(id+"F5.wireOp",EDGE,"E138.top"),sQuery(id+"F5.wireOp",EDGE,"E152")])]});
            var Q3;
            Q3=makeQuery(id+"F6.opExtrude","SWEPT_EDGE",EDGE,{"disambiguationData":[OSD([sQuery(id+"F5.wireOp",EDGE,"E138.bottom"),sQuery(id+"F5.wireOp",EDGE,"E153"),sQuery(id+"F5.wireOp",EDGE,"E176")])]});
            var Q4;
            Q4=makeQuery(id+"F6.opExtrude","SWEPT_EDGE",EDGE,{"disambiguationData":[OSD([sQuery(id+"F5.wireOp",EDGE,"E139.bottom"),sQuery(id+"F5.wireOp",EDGE,"E139.right")])]});
            fillet(context, id + "F7", {"entities" : qUnion([Q0, Q1, Q2, Q3, Q4]), "tangentPropagation" : true, "radius" : 127 * mm, "defaultsChanged" : true, "vertexSettings" : [], "allowEdgeOverflow" : false});
        }
        {
            var Q0;
            Q0=qCreatedBy(makeId("Top.planeOp"),FACE);
            var sketch = newSketch(context, id + "F8", { "sketchPlane" : qUnion([Q0])});
            skLineSegment(sketch, "E191.bottom", {"start": v(-635, -635) * mm, "end": v(635, -635) * mm, "construction": true});
            skLineSegment(sketch, "E191.top", {"start": v(-635, 635) * mm, "end": v(635, 635) * mm, "construction": true});
            skLineSegment(sketch, "E191.left", {"start": v(-635, -635) * mm, "end": v(-635, 635) * mm, "construction": true});
            skLineSegment(sketch, "E191.right", {"start": v(635, -635) * mm, "end": v(635, 635) * mm, "construction": true});
            skPoint(sketch, "E191.middle", {"position": v(0, 0) * mm});
            skPoint(sketch, "E192", {"position": v(-0.02, -635) * mm});
            skLineSegment(sketch, "E193", {"start": v(2284.75, -1201.03) * mm, "end": v(2349.36, -1201.03) * mm});
            skLineSegment(sketch, "E194", {"start": v(2349.36, -1201.03) * mm, "end": v(2385.58, -1101.5) * mm});
            skLineSegment(sketch, "E195", {"start": v(2385.58, -1101.5) * mm, "end": v(2451.68, -1101.5) * mm});
            skLineSegment(sketch, "E196", {"start": v(2451.68, -1101.5) * mm, "end": v(2487.91, -1201.03) * mm});
            skLineSegment(sketch, "E197", {"start": v(2081.59, -1201.03) * mm, "end": v(2146.2, -1201.03) * mm});
            skLineSegment(sketch, "E198", {"start": v(2146.2, -1201.03) * mm, "end": v(2182.42, -1101.5) * mm});
            skLineSegment(sketch, "E199", {"start": v(2182.42, -1101.5) * mm, "end": v(2248.52, -1101.5) * mm});
            skLineSegment(sketch, "E200", {"start": v(2248.52, -1101.5) * mm, "end": v(2284.75, -1201.03) * mm});
            skLineSegment(sketch, "E201", {"start": v(1878.43, -1201.03) * mm, "end": v(1943.03, -1201.03) * mm});
            skLineSegment(sketch, "E202", {"start": v(1943.03, -1201.03) * mm, "end": v(1979.26, -1101.5) * mm});
            skLineSegment(sketch, "E203", {"start": v(1979.26, -1101.5) * mm, "end": v(2045.36, -1101.5) * mm});
            skLineSegment(sketch, "E204", {"start": v(2045.36, -1101.5) * mm, "end": v(2081.59, -1201.03) * mm});
            skLineSegment(sketch, "E205", {"start": v(1675.26, -1201.03) * mm, "end": v(1739.87, -1201.03) * mm});
            skLineSegment(sketch, "E206", {"start": v(1739.87, -1201.03) * mm, "end": v(1776.1, -1101.5) * mm});
            skLineSegment(sketch, "E207", {"start": v(1776.1, -1101.5) * mm, "end": v(1842.2, -1101.5) * mm});
            skLineSegment(sketch, "E208", {"start": v(1842.2, -1101.5) * mm, "end": v(1878.43, -1201.03) * mm});
            skLineSegment(sketch, "E209", {"start": v(1472.1, -1201.03) * mm, "end": v(1536.7, -1201.03) * mm});
            skLineSegment(sketch, "E210", {"start": v(1536.7, -1201.03) * mm, "end": v(1572.94, -1101.5) * mm});
            skLineSegment(sketch, "E211", {"start": v(1572.94, -1101.5) * mm, "end": v(1639.04, -1101.5) * mm});
            skLineSegment(sketch, "E212", {"start": v(1639.04, -1101.5) * mm, "end": v(1675.26, -1201.03) * mm});
            skLineSegment(sketch, "E213", {"start": v(1268.94, -1201.03) * mm, "end": v(1333.55, -1201.03) * mm});
            skLineSegment(sketch, "E214", {"start": v(1333.55, -1201.03) * mm, "end": v(1369.77, -1101.5) * mm});
            skLineSegment(sketch, "E215", {"start": v(1369.77, -1101.5) * mm, "end": v(1435.88, -1101.5) * mm});
            skLineSegment(sketch, "E216", {"start": v(1435.88, -1101.5) * mm, "end": v(1472.1, -1201.03) * mm});
            skLineSegment(sketch, "E217", {"start": v(1065.78, -1201.03) * mm, "end": v(1130.39, -1201.03) * mm});
            skLineSegment(sketch, "E218", {"start": v(1130.39, -1201.03) * mm, "end": v(1166.61, -1101.5) * mm});
            skLineSegment(sketch, "E219", {"start": v(1166.61, -1101.5) * mm, "end": v(1232.71, -1101.5) * mm});
            skLineSegment(sketch, "E220", {"start": v(1232.71, -1101.5) * mm, "end": v(1268.94, -1201.03) * mm});
            skLineSegment(sketch, "E221", {"start": v(862.62, -1201.03) * mm, "end": v(927.22, -1201.03) * mm});
            skLineSegment(sketch, "E222", {"start": v(927.22, -1201.03) * mm, "end": v(963.45, -1101.5) * mm});
            skLineSegment(sketch, "E223", {"start": v(963.45, -1101.5) * mm, "end": v(1029.55, -1101.5) * mm});
            skLineSegment(sketch, "E224", {"start": v(1029.55, -1101.5) * mm, "end": v(1065.78, -1201.03) * mm});
            skLineSegment(sketch, "E225", {"start": v(659.45, -1201.03) * mm, "end": v(724.06, -1201.03) * mm});
            skLineSegment(sketch, "E226", {"start": v(724.06, -1201.03) * mm, "end": v(760.29, -1101.5) * mm});
            skLineSegment(sketch, "E227", {"start": v(760.29, -1101.5) * mm, "end": v(826.4, -1101.5) * mm});
            skLineSegment(sketch, "E228", {"start": v(826.4, -1101.5) * mm, "end": v(862.62, -1201.03) * mm});
            skLineSegment(sketch, "E229", {"start": v(456.3, -1201.03) * mm, "end": v(520.9, -1201.03) * mm});
            skLineSegment(sketch, "E230", {"start": v(520.9, -1201.03) * mm, "end": v(557.13, -1101.5) * mm});
            skLineSegment(sketch, "E231", {"start": v(557.13, -1101.5) * mm, "end": v(623.23, -1101.5) * mm});
            skLineSegment(sketch, "E232", {"start": v(623.23, -1101.5) * mm, "end": v(659.45, -1201.03) * mm});
            skLineSegment(sketch, "E233", {"start": v(253.13, -1201.03) * mm, "end": v(317.74, -1201.03) * mm});
            skLineSegment(sketch, "E234", {"start": v(317.74, -1201.03) * mm, "end": v(353.97, -1101.5) * mm});
            skLineSegment(sketch, "E235", {"start": v(353.97, -1101.5) * mm, "end": v(420.07, -1101.5) * mm});
            skLineSegment(sketch, "E236", {"start": v(420.07, -1101.5) * mm, "end": v(456.3, -1201.03) * mm});
            skLineSegment(sketch, "E237", {"start": v(49.97, -1201.03) * mm, "end": v(114.58, -1201.03) * mm});
            skLineSegment(sketch, "E238", {"start": v(114.58, -1201.03) * mm, "end": v(150.8, -1101.5) * mm});
            skLineSegment(sketch, "E239", {"start": v(150.8, -1101.5) * mm, "end": v(216.9, -1101.5) * mm});
            skLineSegment(sketch, "E240", {"start": v(216.9, -1101.5) * mm, "end": v(253.13, -1201.03) * mm});
            skLineSegment(sketch, "E241", {"start": v(-153.2, -1201.03) * mm, "end": v(-88.58, -1201.03) * mm});
            skLineSegment(sketch, "E242", {"start": v(-88.58, -1201.03) * mm, "end": v(-52.36, -1101.5) * mm});
            skLineSegment(sketch, "E243", {"start": v(-52.36, -1101.5) * mm, "end": v(13.74, -1101.5) * mm});
            skLineSegment(sketch, "E244", {"start": v(13.74, -1101.5) * mm, "end": v(49.97, -1201.03) * mm});
            skLineSegment(sketch, "E245", {"start": v(-356.35, -1201.03) * mm, "end": v(-291.75, -1201.03) * mm});
            skLineSegment(sketch, "E246", {"start": v(-291.75, -1201.03) * mm, "end": v(-255.52, -1101.5) * mm});
            skLineSegment(sketch, "E247", {"start": v(-255.52, -1101.5) * mm, "end": v(-189.42, -1101.5) * mm});
            skLineSegment(sketch, "E248", {"start": v(-189.42, -1101.5) * mm, "end": v(-153.2, -1201.03) * mm});
            skLineSegment(sketch, "E249", {"start": v(-559.52, -1201.03) * mm, "end": v(-494.9, -1201.03) * mm});
            skLineSegment(sketch, "E250", {"start": v(-494.9, -1201.03) * mm, "end": v(-458.68, -1101.5) * mm});
            skLineSegment(sketch, "E251", {"start": v(-458.68, -1101.5) * mm, "end": v(-392.58, -1101.5) * mm});
            skLineSegment(sketch, "E252", {"start": v(-392.58, -1101.5) * mm, "end": v(-356.35, -1201.03) * mm});
            skLineSegment(sketch, "E253", {"start": v(-762.68, -1201.03) * mm, "end": v(-698.07, -1201.03) * mm});
            skLineSegment(sketch, "E254", {"start": v(-698.07, -1201.03) * mm, "end": v(-661.84, -1101.5) * mm});
            skLineSegment(sketch, "E255", {"start": v(-661.84, -1101.5) * mm, "end": v(-595.74, -1101.5) * mm});
            skLineSegment(sketch, "E256", {"start": v(-595.74, -1101.5) * mm, "end": v(-559.52, -1201.03) * mm});
            skLineSegment(sketch, "E257", {"start": v(-965.84, -1201.03) * mm, "end": v(-901.23, -1201.03) * mm});
            skLineSegment(sketch, "E258", {"start": v(-901.23, -1201.03) * mm, "end": v(-865, -1101.5) * mm});
            skLineSegment(sketch, "E259", {"start": v(-865, -1101.5) * mm, "end": v(-798.9, -1101.5) * mm});
            skLineSegment(sketch, "E260", {"start": v(-798.9, -1101.5) * mm, "end": v(-762.68, -1201.03) * mm});
            skLineSegment(sketch, "E261", {"start": v(-1169, -1201.03) * mm, "end": v(-1104.4, -1201.03) * mm});
            skLineSegment(sketch, "E262", {"start": v(-1104.4, -1201.03) * mm, "end": v(-1068.17, -1101.5) * mm});
            skLineSegment(sketch, "E263", {"start": v(-1068.17, -1101.5) * mm, "end": v(-1002.07, -1101.5) * mm});
            skLineSegment(sketch, "E264", {"start": v(-1002.07, -1101.5) * mm, "end": v(-965.84, -1201.03) * mm});
            skLineSegment(sketch, "E265", {"start": v(-1372.16, -1201.03) * mm, "end": v(-1307.55, -1201.03) * mm});
            skLineSegment(sketch, "E266", {"start": v(-1307.55, -1201.03) * mm, "end": v(-1271.33, -1101.5) * mm});
            skLineSegment(sketch, "E267", {"start": v(-1271.33, -1101.5) * mm, "end": v(-1205.23, -1101.5) * mm});
            skLineSegment(sketch, "E268", {"start": v(-1205.23, -1101.5) * mm, "end": v(-1169, -1201.03) * mm});
            skLineSegment(sketch, "E269", {"start": v(-1575.32, -1201.03) * mm, "end": v(-1510.72, -1201.03) * mm});
            skLineSegment(sketch, "E270", {"start": v(-1510.72, -1201.03) * mm, "end": v(-1474.5, -1101.5) * mm});
            skLineSegment(sketch, "E271", {"start": v(-1474.5, -1101.5) * mm, "end": v(-1408.39, -1101.5) * mm});
            skLineSegment(sketch, "E272", {"start": v(-1408.39, -1101.5) * mm, "end": v(-1372.16, -1201.03) * mm});
            skLineSegment(sketch, "E273", {"start": v(-1778.49, -1201.03) * mm, "end": v(-1713.88, -1201.03) * mm});
            skLineSegment(sketch, "E274", {"start": v(-1713.88, -1201.03) * mm, "end": v(-1677.65, -1101.5) * mm});
            skLineSegment(sketch, "E275", {"start": v(-1677.65, -1101.5) * mm, "end": v(-1611.55, -1101.5) * mm});
            skLineSegment(sketch, "E276", {"start": v(-1611.55, -1101.5) * mm, "end": v(-1575.32, -1201.03) * mm});
            skLineSegment(sketch, "E277", {"start": v(-1981.65, -1201.03) * mm, "end": v(-1917.04, -1201.03) * mm});
            skLineSegment(sketch, "E278", {"start": v(-1917.04, -1201.03) * mm, "end": v(-1880.81, -1101.5) * mm});
            skLineSegment(sketch, "E279", {"start": v(-1880.81, -1101.5) * mm, "end": v(-1814.71, -1101.5) * mm});
            skLineSegment(sketch, "E280", {"start": v(-1814.71, -1101.5) * mm, "end": v(-1778.49, -1201.03) * mm});
            skLineSegment(sketch, "E281", {"start": v(-2184.81, -1201.03) * mm, "end": v(-2120.2, -1201.03) * mm});
            skLineSegment(sketch, "E282", {"start": v(-2120.2, -1201.03) * mm, "end": v(-2083.98, -1101.5) * mm});
            skLineSegment(sketch, "E283", {"start": v(-2083.98, -1101.5) * mm, "end": v(-2017.87, -1101.5) * mm});
            skLineSegment(sketch, "E284", {"start": v(-2017.87, -1101.5) * mm, "end": v(-1981.65, -1201.03) * mm});
            skLineSegment(sketch, "E285", {"start": v(-2388.2, -1201.03) * mm, "end": v(-2323.36, -1201.03) * mm});
            skLineSegment(sketch, "E286", {"start": v(-2323.36, -1201.03) * mm, "end": v(-2287.14, -1101.5) * mm});
            skLineSegment(sketch, "E287", {"start": v(-2287.14, -1101.5) * mm, "end": v(-2221.04, -1101.5) * mm});
            skLineSegment(sketch, "E288", {"start": v(-2221.04, -1101.5) * mm, "end": v(-2184.81, -1201.03) * mm});
            skLineSegment(sketch, "E289", {"start": v(-2491.46, -1101.5) * mm, "end": v(-2424.43, -1101.5) * mm});
            skLineSegment(sketch, "E290", {"start": v(-2424.43, -1101.5) * mm, "end": v(-2388.2, -1201.03) * mm});
            skCircle(sketch, "E291", {"center": v(-3387.26, -850.9) * mm, "radius": 50.8 * mm});
            skLineSegment(sketch, "E292", {"start": v(-2592.51, -1201.07) * mm, "end": v(-2527.69, -1201.03) * mm});
            skLineSegment(sketch, "E293", {"start": v(-2527.69, -1201.03) * mm, "end": v(-2491.46, -1101.5) * mm});
            skLineSegment(sketch, "E294", {"start": v(-2629.3, -1101.5) * mm, "end": v(-2592.51, -1201.07) * mm});
            skLineSegment(sketch, "E295", {"start": v(-2696.33, -1101.5) * mm, "end": v(-2629.3, -1101.5) * mm});
            skLineSegment(sketch, "E296", {"start": v(-2733.1, -1201.03) * mm, "end": v(-2696.33, -1101.5) * mm});
            skLineSegment(sketch, "E297", {"start": v(2691.8, -1201.03) * mm, "end": v(2757.13, -1201.03) * mm});
            skLineSegment(sketch, "E298", {"start": v(2757.13, -1201.03) * mm, "end": v(2794, -1101.35) * mm});
            skLineSegment(sketch, "E299", {"start": v(2655.57, -1101.5) * mm, "end": v(2691.8, -1201.03) * mm});
            skLineSegment(sketch, "E300", {"start": v(-2794.02, -1201.07) * mm, "end": v(-2733.1, -1201.03) * mm});
            skCircle(sketch, "E301", {"center": v(-2980.94, -850.9) * mm, "radius": 80.01 * mm});
            skCircle(sketch, "E302", {"center": v(2972.28, -850.9) * mm, "radius": 80.01 * mm});
            skLineSegment(sketch, "E303", {"start": v(-2980.94, -770.9) * mm, "end": v(2972.28, -770.89) * mm});
            skLineSegment(sketch, "E304", {"start": v(2972.28, -930.9) * mm, "end": v(-2980.94, -930.9) * mm});
            skLineSegment(sketch, "E305.bottom", {"start": v(-2794.02, -635) * mm, "end": v(2793.98, -635) * mm});
            skLineSegment(sketch, "E305.top", {"start": v(-2794.02, -1176.6) * mm, "end": v(3200.88, -1176.6) * mm, "construction": true});
            skLineSegment(sketch, "E305.left", {"start": v(-2794.02, -635) * mm, "end": v(-2794.02, -1176.6) * mm});
            skLineSegment(sketch, "E306", {"start": v(-2794.02, -1201.07) * mm, "end": v(-2794.02, -1176.6) * mm});
            skLineSegment(sketch, "E307.bottom", {"start": v(-2794.02, -635) * mm, "end": v(-3615.94, -635) * mm});
            skLineSegment(sketch, "E307.top", {"start": v(-2794.02, -1092.2) * mm, "end": v(-3615.94, -1092.2) * mm});
            skLineSegment(sketch, "E307.left", {"start": v(-2794.02, -635) * mm, "end": v(-2794.02, -1092.2) * mm});
            skLineSegment(sketch, "E307.right", {"start": v(-3615.94, -635) * mm, "end": v(-3615.94, -1092.2) * mm});
            skLineSegment(sketch, "E308.bottom", {"start": v(2793.98, -635) * mm, "end": v(3200.88, -635) * mm});
            skLineSegment(sketch, "E308.right", {"start": v(3200.88, -635) * mm, "end": v(3200.88, -1267.09) * mm});
            skPoint(sketch, "E309", {"position": v(2746.58, -635) * mm});
            skLineSegment(sketch, "E310", {"start": v(2896.33, -1200.88) * mm, "end": v(2961.66, -1200.88) * mm});
            skLineSegment(sketch, "E311", {"start": v(2961.66, -1200.88) * mm, "end": v(2998.53, -1101.2) * mm});
            skLineSegment(sketch, "E312", {"start": v(2794, -1101.35) * mm, "end": v(2860.1, -1101.35) * mm});
            skLineSegment(sketch, "E313", {"start": v(2860.1, -1101.35) * mm, "end": v(2896.33, -1200.88) * mm});
            skLineSegment(sketch, "E314", {"start": v(3100.86, -1200.74) * mm, "end": v(3166.2, -1200.74) * mm});
            skLineSegment(sketch, "E315", {"start": v(3166.2, -1200.74) * mm, "end": v(3200.88, -1100.56) * mm});
            skLineSegment(sketch, "E316", {"start": v(2998.53, -1101.2) * mm, "end": v(3064.63, -1101.2) * mm});
            skLineSegment(sketch, "E317", {"start": v(3064.63, -1101.2) * mm, "end": v(3100.86, -1200.74) * mm});
            skPoint(sketch, "E318", {"position": v(3200.88, -1176.6) * mm});
            skPoint(sketch, "E319", {"position": v(-2980.94, -635) * mm});
            skCircle(sketch, "E320", {"center": v(0, 0) * mm, "radius": 3302 * mm});
            skCircle(sketch, "E321", {"center": v(0, 0) * mm, "radius": 3683 * mm});
            skCircle(sketch, "E322", {"center": v(0, 0) * mm, "radius": 3492.5 * mm, "construction": true});
            skLineSegment(sketch, "E323", {"start": v(-2980.94, -850.9) * mm, "end": v(-3615.94, -850.9) * mm, "construction": true});
            skLineSegment(sketch, "E324", {"start": v(0, 0) * mm, "end": v(-3683, 0) * mm, "construction": true});
            skCircle(sketch, "E325", {"center": v(-3492.5, 0) * mm, "radius": 50.8 * mm});
            skLineSegment(sketch, "E326", {"start": v(0, 0) * mm, "end": v(-3674.03, 256.91) * mm});
            skLineSegment(sketch, "E327", {"start": v(-3387.26, -850.9) * mm, "end": v(0, 0) * mm, "construction": true});
            skLineSegment(sketch, "E328.bottom", {"start": v(-3674.03, -1267.09) * mm, "end": v(4453.97, -1267.09) * mm, "construction": true});
            skLineSegment(sketch, "E328.top", {"start": v(-3674.03, 256.91) * mm, "end": v(4453.97, 256.91) * mm, "construction": true});
            skLineSegment(sketch, "E328.left", {"start": v(-3674.03, -1267.09) * mm, "end": v(-3674.03, 256.91) * mm, "construction": true});
            skLineSegment(sketch, "E328.right", {"start": v(4453.97, -1267.09) * mm, "end": v(4453.97, 256.91) * mm, "construction": true});
            skCircle(sketch, "E329", {"center": v(0, 0) * mm, "radius": 4064 * mm});
            skCircle(sketch, "E330", {"center": v(0, 0) * mm, "radius": 3810 * mm});
            skLineSegment(sketch, "E331", {"start": v(-3683, 0) * mm, "end": v(-3683, -228.6) * mm});
            skLineSegment(sketch, "E332", {"start": v(-3683, -228.6) * mm, "end": v(-3273.6, -432.13) * mm});
            skLineSegment(sketch, "E333", {"start": v(-3235.22, -660.73) * mm, "end": v(-3652, -1085.83) * mm});
            skLineSegment(sketch, "E334", {"start": v(-3615.94, -1092.2) * mm, "end": v(-3650.1, -1092.2) * mm});
            skLineSegment(sketch, "E335.bottom", {"start": v(-3107.94, -635) * mm, "end": v(-2726.94, -635) * mm});
            skLineSegment(sketch, "E335.top", {"start": v(-3107.94, -254) * mm, "end": v(-2726.94, -254) * mm});
            skLineSegment(sketch, "E335.left", {"start": v(-3107.94, -635) * mm, "end": v(-3107.94, -254) * mm, "construction": true});
            skLineSegment(sketch, "E335.right", {"start": v(-2726.94, -635) * mm, "end": v(-2726.94, -254) * mm});
            skPoint(sketch, "E336", {"position": v(-2794.02, -635) * mm});
            skLineSegment(sketch, "E337", {"start": v(2487.91, -1201.03) * mm, "end": v(2552.52, -1201.03) * mm});
            skLineSegment(sketch, "E338", {"start": v(2552.52, -1201.03) * mm, "end": v(2588.74, -1101.5) * mm});
            skLineSegment(sketch, "E339", {"start": v(2588.74, -1101.5) * mm, "end": v(2655.57, -1101.5) * mm});
            skLineSegment(sketch, "E340", {"start": v(-3107.94, -254) * mm, "end": v(-3292.22, -254) * mm});
            skSolve(sketch);
        }
        {
            var Q0;
            Q0=makeQuery(id+"F8.imprint","IMPRINT",FACE,{"disambiguationData":[TD([[makeQuery(id+"F8.imprint","IMPRINT",EDGE,{"derivedFrom":sQuery(id+"F8.wireOp",EDGE,"8a0a596a-1b78-45c2-80a2-c71a9cac3839")}),1.0]])]});
            var Q1;
            Q1=makeQuery(id+"F8.imprint","IMPRINT",FACE,{"disambiguationData":[TD([[makeQuery(id+"F8.imprint","IMPRINT",EDGE,{"derivedFrom":sQuery(id+"F8.wireOp",EDGE,"E335.top")}),-1.0]])]});
            var Q2;
            {var subQ5=sQuery(id+"F8.wireOp",EDGE,"E303");var subQ6=sQuery(id+"F8.wireOp",EDGE,"E301");var subQ7=makeQuery(id+"F8.imprint","INTERSECT",VERTEX,{"derivedFrom":[subQ6,subQ5]});Q2=makeQuery(id+"F8.imprint","IMPRINT",FACE,{"disambiguationData":[TD([[makeQuery(id+"F8.imprint","IMPRINT",EDGE,{"disambiguationData":[TD([[subQ7,-1.0]])],"derivedFrom":subQ6}),-1.0]])]});}
            var Q3;
            {var subQ3=sQuery(id+"F8.wireOp",EDGE,"E333");var subQ8=sQuery(id+"F8.wireOp",EDGE,"E291");var subQ9=makeQuery(id+"F8.imprint","INTERSECT",VERTEX,{"disambiguationData":[OD(0.0)],"derivedFrom":[subQ8,subQ3]});Q3=makeQuery(id+"F8.imprint","IMPRINT",FACE,{"disambiguationData":[TD([[makeQuery(id+"F8.imprint","IMPRINT",EDGE,{"disambiguationData":[TD([[subQ9,1.0]])],"derivedFrom":subQ8}),-1.0]])]});}
            var Q4;
            {var subQ0=sQuery(id+"F8.wireOp",EDGE,"E333");var subQ9=sQuery(id+"F8.wireOp",EDGE,"E291");var subQ10=makeQuery(id+"F8.imprint","INTERSECT",VERTEX,{"disambiguationData":[OD(0.0)],"derivedFrom":[subQ9,subQ0]});Q4=makeQuery(id+"F8.imprint","IMPRINT",FACE,{"disambiguationData":[TD([[makeQuery(id+"F8.imprint","IMPRINT",EDGE,{"disambiguationData":[TD([[subQ10,-1.0]])],"derivedFrom":subQ9}),-1.0]])]});}
            var Q5;
            {var subQ0=sQuery(id+"F8.wireOp",EDGE,"E333");var subQ1=sQuery(id+"F8.wireOp",EDGE,"E291");var subQ2=makeQuery(id+"F8.imprint","INTERSECT",VERTEX,{"disambiguationData":[OD(0.0)],"derivedFrom":[subQ1,subQ0]});Q5=makeQuery(id+"F8.imprint","IMPRINT",FACE,{"disambiguationData":[TD([[makeQuery(id+"F8.imprint","IMPRINT",EDGE,{"disambiguationData":[TD([[subQ2,1.0]])],"derivedFrom":subQ1}),1.0]])]});}
            var Q6;
            {var subQ0=sQuery(id+"F8.wireOp",EDGE,"E333");var subQ1=sQuery(id+"F8.wireOp",EDGE,"E291");var subQ2=makeQuery(id+"F8.imprint","INTERSECT",VERTEX,{"disambiguationData":[OD(0.0)],"derivedFrom":[subQ1,subQ0]});Q6=makeQuery(id+"F8.imprint","IMPRINT",FACE,{"disambiguationData":[TD([[makeQuery(id+"F8.imprint","IMPRINT",EDGE,{"disambiguationData":[TD([[subQ2,-1.0]])],"derivedFrom":subQ1}),1.0]])]});}
            var Q7;
            {var subQ1=sQuery(id+"F8.wireOp",EDGE,"E307.right");var subQ7=sQuery(id+"F8.wireOp",EDGE,"E307.bottom");var subQ9=makeQuery(id+"F8.imprint","INTERSECT",VERTEX,{"derivedFrom":[subQ7,subQ1]});Q7=makeQuery(id+"F8.imprint","IMPRINT",FACE,{"disambiguationData":[TD([[makeQuery(id+"F8.imprint","IMPRINT",EDGE,{"disambiguationData":[TD([[subQ9,1.0]])],"derivedFrom":subQ7}),-1.0]])]});}
            var Q8;
            {var subQ1=sQuery(id+"F8.wireOp",EDGE,"E314");Q8=makeQuery(id+"F8.imprint","IMPRINT",FACE,{"disambiguationData":[TD([[makeQuery(id+"F8.imprint","IMPRINT",EDGE,{"derivedFrom":subQ1}),1.0]])]});}
            var Q9;
            Q9=makeQuery(id+"F8.imprint","IMPRINT",FACE,{"disambiguationData":[TD([[makeQuery(id+"F8.imprint","IMPRINT",EDGE,{"derivedFrom":sQuery(id+"F8.wireOp",EDGE,"E193")}),1.0]])]});
            extrude(context, id + "F9", {"entities" : qUnion([Q0, Q1, Q2, Q3, Q4, Q5, Q6, Q7, Q8, Q9]), "depth" : 152.4 * mm, "offsetDistance" : 25.4 * mm});
        }
        {
            var Q0;
            Q0=makeQuery(id+"F9.opExtrude","SWEPT_EDGE",EDGE,{"disambiguationData":[OSD([sQuery(id+"F8.wireOp",EDGE,"E307.top"),sQuery(id+"F8.wireOp",EDGE,"E321")])]});
            var Q1;
            Q1=makeQuery(id+"F9.opExtrude","SWEPT_EDGE",EDGE,{"disambiguationData":[OSD([sQuery(id+"F8.wireOp",EDGE,"E321"),sQuery(id+"F8.wireOp",EDGE,"E332")])]});
            var Q2;
            Q2=makeQuery(id+"F9.opExtrude","SWEPT_EDGE",EDGE,{"disambiguationData":[OSD([sQuery(id+"F8.wireOp",EDGE,"E307.bottom"),sQuery(id+"F8.wireOp",EDGE,"E335.bottom"),sQuery(id+"F8.wireOp",EDGE,"E335.left")])]});
            var Q3;
            Q3=makeQuery(id+"F9.opExtrude","SWEPT_EDGE",EDGE,{"disambiguationData":[OSD([sQuery(id+"F8.wireOp",EDGE,"E335.top"),sQuery(id+"F8.wireOp",EDGE,"E335.left")])]});
            var Q4;
            Q4=makeQuery(id+"F9.opExtrude","SWEPT_EDGE",EDGE,{"disambiguationData":[OSD([sQuery(id+"F8.wireOp",EDGE,"E335.top"),sQuery(id+"F8.wireOp",EDGE,"E335.right")])]});
            var Q5;
            Q5=makeQuery(id+"F9.opExtrude","SWEPT_EDGE",EDGE,{"disambiguationData":[OSD([sQuery(id+"F8.wireOp",EDGE,"E305.bottom"),sQuery(id+"F8.wireOp",EDGE,"E335.bottom"),sQuery(id+"F8.wireOp",EDGE,"E335.right")])]});
            var Q6;
            Q6=makeQuery(id+"F9.opExtrude","SWEPT_EDGE",EDGE,{"disambiguationData":[OSD([sQuery(id+"F8.wireOp",EDGE,"E308.bottom"),sQuery(id+"F8.wireOp",EDGE,"E308.right")])]});
            var Q7;
            Q7=makeQuery(id+"F9.opExtrude","SWEPT_EDGE",EDGE,{"disambiguationData":[OSD([sQuery(id+"F8.wireOp",EDGE,"E320"),sQuery(id+"F8.wireOp",EDGE,"E332")])]});
            fillet(context, id + "F10", {"entities" : qUnion([Q0, Q1, Q2, Q3, Q4, Q5, Q6, Q7]), "tangentPropagation" : true, "radius" : 127 * mm, "defaultsChanged" : false, "vertexSettings" : [], "allowEdgeOverflow" : false});
        }
        {
            var Q0;
            Q0=makeQuery(id+"F8.imprint","IMPRINT",FACE,{"disambiguationData":[TD([[makeQuery(id+"F8.imprint","IMPRINT",EDGE,{"derivedFrom":sQuery(id+"F8.wireOp",EDGE,"8a0a596a-1b78-45c2-80a2-c71a9cac3839")}),1.0]])]});
            var Q1;
            {var subQ5=sQuery(id+"F8.wireOp",EDGE,"E303");var subQ6=sQuery(id+"F8.wireOp",EDGE,"E301");var subQ7=makeQuery(id+"F8.imprint","INTERSECT",VERTEX,{"derivedFrom":[subQ6,subQ5]});Q1=makeQuery(id+"F8.imprint","IMPRINT",FACE,{"disambiguationData":[TD([[makeQuery(id+"F8.imprint","IMPRINT",EDGE,{"disambiguationData":[TD([[subQ7,-1.0]])],"derivedFrom":subQ6}),-1.0]])]});}
            var Q2;
            {var subQ3=sQuery(id+"F8.wireOp",EDGE,"E333");var subQ8=sQuery(id+"F8.wireOp",EDGE,"E291");var subQ9=makeQuery(id+"F8.imprint","INTERSECT",VERTEX,{"disambiguationData":[OD(0.0)],"derivedFrom":[subQ8,subQ3]});Q2=makeQuery(id+"F8.imprint","IMPRINT",FACE,{"disambiguationData":[TD([[makeQuery(id+"F8.imprint","IMPRINT",EDGE,{"disambiguationData":[TD([[subQ9,1.0]])],"derivedFrom":subQ8}),-1.0]])]});}
            var Q3;
            {var subQ0=sQuery(id+"F8.wireOp",EDGE,"E333");var subQ9=sQuery(id+"F8.wireOp",EDGE,"E291");var subQ10=makeQuery(id+"F8.imprint","INTERSECT",VERTEX,{"disambiguationData":[OD(0.0)],"derivedFrom":[subQ9,subQ0]});Q3=makeQuery(id+"F8.imprint","IMPRINT",FACE,{"disambiguationData":[TD([[makeQuery(id+"F8.imprint","IMPRINT",EDGE,{"disambiguationData":[TD([[subQ10,-1.0]])],"derivedFrom":subQ9}),-1.0]])]});}
            var Q4;
            {var subQ0=sQuery(id+"F8.wireOp",EDGE,"E333");var subQ1=sQuery(id+"F8.wireOp",EDGE,"E291");var subQ2=makeQuery(id+"F8.imprint","INTERSECT",VERTEX,{"disambiguationData":[OD(0.0)],"derivedFrom":[subQ1,subQ0]});Q4=makeQuery(id+"F8.imprint","IMPRINT",FACE,{"disambiguationData":[TD([[makeQuery(id+"F8.imprint","IMPRINT",EDGE,{"disambiguationData":[TD([[subQ2,1.0]])],"derivedFrom":subQ1}),1.0]])]});}
            var Q5;
            {var subQ0=sQuery(id+"F8.wireOp",EDGE,"E333");var subQ1=sQuery(id+"F8.wireOp",EDGE,"E291");var subQ2=makeQuery(id+"F8.imprint","INTERSECT",VERTEX,{"disambiguationData":[OD(0.0)],"derivedFrom":[subQ1,subQ0]});Q5=makeQuery(id+"F8.imprint","IMPRINT",FACE,{"disambiguationData":[TD([[makeQuery(id+"F8.imprint","IMPRINT",EDGE,{"disambiguationData":[TD([[subQ2,-1.0]])],"derivedFrom":subQ1}),1.0]])]});}
            var Q6;
            {var subQ1=sQuery(id+"F8.wireOp",EDGE,"E314");Q6=makeQuery(id+"F8.imprint","IMPRINT",FACE,{"disambiguationData":[TD([[makeQuery(id+"F8.imprint","IMPRINT",EDGE,{"derivedFrom":subQ1}),1.0]])]});}
            var Q7;
            {var subQ1=sQuery(id+"F8.wireOp",EDGE,"E307.right");var subQ7=sQuery(id+"F8.wireOp",EDGE,"E307.bottom");var subQ9=makeQuery(id+"F8.imprint","INTERSECT",VERTEX,{"derivedFrom":[subQ7,subQ1]});Q7=makeQuery(id+"F8.imprint","IMPRINT",FACE,{"disambiguationData":[TD([[makeQuery(id+"F8.imprint","IMPRINT",EDGE,{"disambiguationData":[TD([[subQ9,1.0]])],"derivedFrom":subQ7}),-1.0]])]});}
            var Q8;
            Q8=makeQuery(id+"F8.imprint","IMPRINT",FACE,{"disambiguationData":[TD([[makeQuery(id+"F8.imprint","IMPRINT",EDGE,{"derivedFrom":sQuery(id+"F8.wireOp",EDGE,"E193")}),1.0]])]});
            extrude(context, id + "F11", {"entities" : qUnion([Q0, Q1, Q2, Q3, Q4, Q5, Q6, Q7, Q8]), "depth" : 152.4 * mm, "offsetDistance" : 25.4 * mm});
        }
        {
            var Q0;
            Q0=makeQuery(id+"F11.opExtrude","SWEPT_EDGE",EDGE,{"disambiguationData":[OSD([sQuery(id+"F8.wireOp",EDGE,"E307.top"),sQuery(id+"F8.wireOp",EDGE,"E321")])]});
            var Q1;
            Q1=makeQuery(id+"F11.opExtrude","SWEPT_EDGE",EDGE,{"disambiguationData":[OSD([sQuery(id+"F8.wireOp",EDGE,"E321"),sQuery(id+"F8.wireOp",EDGE,"E332")])]});
            var Q2;
            Q2=makeQuery(id+"F11.opExtrude","SWEPT_EDGE",EDGE,{"disambiguationData":[OSD([sQuery(id+"F8.wireOp",EDGE,"E320"),sQuery(id+"F8.wireOp",EDGE,"E332")])]});
            var Q3;
            Q3=makeQuery(id+"F11.opExtrude","SWEPT_EDGE",EDGE,{"disambiguationData":[OSD([sQuery(id+"F8.wireOp",EDGE,"E307.bottom"),sQuery(id+"F8.wireOp",EDGE,"E320")])]});
            var Q4;
            Q4=makeQuery(id+"F11.opExtrude","SWEPT_EDGE",EDGE,{"disambiguationData":[OSD([sQuery(id+"F8.wireOp",EDGE,"E308.bottom"),sQuery(id+"F8.wireOp",EDGE,"E308.right")])]});
            fillet(context, id + "F12", {"entities" : qUnion([Q0, Q1, Q2, Q3, Q4]), "tangentPropagation" : true, "radius" : 127 * mm, "defaultsChanged" : true, "vertexSettings" : [], "allowEdgeOverflow" : false});
        }
        {
            var Q0;
            {var subQ0=sQuery(id+"F8.wireOp",EDGE,"E333");var subQ9=sQuery(id+"F8.wireOp",EDGE,"E291");var subQ10=makeQuery(id+"F8.imprint","INTERSECT",VERTEX,{"disambiguationData":[OD(0.0)],"derivedFrom":[subQ9,subQ0]});Q0=makeQuery(id+"F8.imprint","IMPRINT",FACE,{"disambiguationData":[TD([[makeQuery(id+"F8.imprint","IMPRINT",EDGE,{"disambiguationData":[TD([[subQ10,-1.0]])],"derivedFrom":subQ9}),-1.0]])]});}
            var Q1;
            {var subQ1=sQuery(id+"F8.wireOp",EDGE,"E307.right");var subQ7=sQuery(id+"F8.wireOp",EDGE,"E307.bottom");var subQ9=makeQuery(id+"F8.imprint","INTERSECT",VERTEX,{"derivedFrom":[subQ7,subQ1]});Q1=makeQuery(id+"F8.imprint","IMPRINT",FACE,{"disambiguationData":[TD([[makeQuery(id+"F8.imprint","IMPRINT",EDGE,{"disambiguationData":[TD([[subQ9,1.0]])],"derivedFrom":subQ7}),-1.0]])]});}
            var Q2;
            {var subQ3=sQuery(id+"F8.wireOp",EDGE,"E333");var subQ8=sQuery(id+"F8.wireOp",EDGE,"E291");var subQ9=makeQuery(id+"F8.imprint","INTERSECT",VERTEX,{"disambiguationData":[OD(0.0)],"derivedFrom":[subQ8,subQ3]});Q2=makeQuery(id+"F8.imprint","IMPRINT",FACE,{"disambiguationData":[TD([[makeQuery(id+"F8.imprint","IMPRINT",EDGE,{"disambiguationData":[TD([[subQ9,1.0]])],"derivedFrom":subQ8}),-1.0]])]});}
            var Q3;
            {var subQ0=sQuery(id+"F8.wireOp",EDGE,"E333");var subQ1=sQuery(id+"F8.wireOp",EDGE,"E291");var subQ2=makeQuery(id+"F8.imprint","INTERSECT",VERTEX,{"disambiguationData":[OD(0.0)],"derivedFrom":[subQ1,subQ0]});Q3=makeQuery(id+"F8.imprint","IMPRINT",FACE,{"disambiguationData":[TD([[makeQuery(id+"F8.imprint","IMPRINT",EDGE,{"disambiguationData":[TD([[subQ2,1.0]])],"derivedFrom":subQ1}),1.0]])]});}
            var Q4;
            {var subQ0=sQuery(id+"F8.wireOp",EDGE,"E333");var subQ1=sQuery(id+"F8.wireOp",EDGE,"E291");var subQ2=makeQuery(id+"F8.imprint","INTERSECT",VERTEX,{"disambiguationData":[OD(0.0)],"derivedFrom":[subQ1,subQ0]});Q4=makeQuery(id+"F8.imprint","IMPRINT",FACE,{"disambiguationData":[TD([[makeQuery(id+"F8.imprint","IMPRINT",EDGE,{"disambiguationData":[TD([[subQ2,-1.0]])],"derivedFrom":subQ1}),1.0]])]});}
            extrude(context, id + "F13", {"entities" : qUnion([Q0, Q1, Q2, Q3, Q4]), "depth" : 152.4 * mm, "offsetDistance" : 25.4 * mm});
        }
        {
            var Q0;
            Q0=makeQuery(id+"F13.opExtrude","SWEPT_EDGE",EDGE,{"disambiguationData":[OSD([sQuery(id+"F8.wireOp",EDGE,"E320"),sQuery(id+"F8.wireOp",EDGE,"E332")])]});
            var Q1;
            Q1=makeQuery(id+"F13.opExtrude","SWEPT_EDGE",EDGE,{"disambiguationData":[OSD([sQuery(id+"F8.wireOp",EDGE,"E321"),sQuery(id+"F8.wireOp",EDGE,"E332")])]});
            var Q2;
            Q2=makeQuery(id+"F13.opExtrude","SWEPT_EDGE",EDGE,{"disambiguationData":[OSD([sQuery(id+"F8.wireOp",EDGE,"E307.top"),sQuery(id+"F8.wireOp",EDGE,"E321")])]});
            fillet(context, id + "F14", {"entities" : qUnion([Q0, Q1, Q2]), "tangentPropagation" : true, "radius" : 127 * mm, "defaultsChanged" : true, "vertexSettings" : [], "allowEdgeOverflow" : false});
        }
        {
            var Q0;
            {var subQ0=sQuery(id+"F5.wireOp",EDGE,"E189");var subQ1=sQuery(id+"F5.wireOp",EDGE,"E152");var subQ2=makeQuery(id+"F5.imprint","INTERSECT",VERTEX,{"derivedFrom":[subQ1,subQ0]});Q0=makeQuery(id+"F5.imprint","IMPRINT",FACE,{"disambiguationData":[TD([[makeQuery(id+"F5.imprint","IMPRINT",EDGE,{"disambiguationData":[TD([[subQ2,1.0]])],"derivedFrom":subQ1}),-1.0]])]});}
            var Q1;
            {var subQ1=sQuery(id+"F5.wireOp",EDGE,"E138.right");var subQ9=sQuery(id+"F5.wireOp",EDGE,"E138.top");var subQ10=makeQuery(id+"F5.imprint","INTERSECT",VERTEX,{"derivedFrom":[subQ9,subQ1]});Q1=makeQuery(id+"F5.imprint","IMPRINT",FACE,{"disambiguationData":[TD([[makeQuery(id+"F5.imprint","IMPRINT",EDGE,{"disambiguationData":[TD([[subQ10,1.0]])],"derivedFrom":subQ9}),1.0]])]});}
            var Q2;
            Q2=makeQuery(id+"F5.imprint","IMPRINT",FACE,{"disambiguationData":[TD([[makeQuery(id+"F5.imprint","IMPRINT",EDGE,{"derivedFrom":sQuery(id+"F5.wireOp",EDGE,"E125")}),-1.0]])]});
            var Q3;
            {var subQ0=sQuery(id+"F5.wireOp",EDGE,"E138.right");var subQ1=sQuery(id+"F5.wireOp",EDGE,"E138.top");var subQ2=makeQuery(id+"F5.imprint","INTERSECT",VERTEX,{"derivedFrom":[subQ1,subQ0]});Q3=makeQuery(id+"F5.imprint","IMPRINT",FACE,{"disambiguationData":[TD([[makeQuery(id+"F5.imprint","IMPRINT",EDGE,{"disambiguationData":[TD([[subQ2,1.0]])],"derivedFrom":subQ1}),-1.0]])]});}
            var Q4;
            {var subQ0=sQuery(id+"F5.wireOp",EDGE,"E152");var subQ1=sQuery(id+"F5.wireOp",EDGE,"E138.top");var subQ2=makeQuery(id+"F5.imprint","INTERSECT",VERTEX,{"derivedFrom":[subQ1,subQ0]});Q4=makeQuery(id+"F5.imprint","IMPRINT",FACE,{"disambiguationData":[TD([[makeQuery(id+"F5.imprint","IMPRINT",EDGE,{"disambiguationData":[TD([[subQ2,-1.0]])],"derivedFrom":subQ1}),1.0]])]});}
            var Q5;
            {var subQ0=sQuery(id+"F5.wireOp",EDGE,"E152");var subQ1=sQuery(id+"F5.wireOp",EDGE,"E138.bottom");var subQ2=makeQuery(id+"F5.imprint","INTERSECT",VERTEX,{"derivedFrom":[subQ1,subQ0]});Q5=makeQuery(id+"F5.imprint","IMPRINT",FACE,{"disambiguationData":[TD([[makeQuery(id+"F5.imprint","IMPRINT",EDGE,{"disambiguationData":[TD([[subQ2,-1.0]])],"derivedFrom":subQ1}),1.0]])]});}
            var Q6;
            Q6=makeQuery(id+"F5.imprint","IMPRINT",FACE,{"disambiguationData":[TD([[makeQuery(id+"F5.imprint","IMPRINT",EDGE,{"derivedFrom":sQuery(id+"F5.wireOp",EDGE,"E125")}),1.0]])]});
            extrude(context, id + "F15", {"entities" : qUnion([Q0, Q1, Q2, Q3, Q4, Q5, Q6]), "depth" : 152.4 * mm, "offsetDistance" : 25.4 * mm});
        }
        {
            var Q0;
            Q0=makeQuery(id+"F15.opExtrude","SWEPT_EDGE",EDGE,{"disambiguationData":[OSD([sQuery(id+"F5.wireOp",EDGE,"E153"),sQuery(id+"F5.wireOp",EDGE,"E189")])]});
            var Q1;
            Q1=makeQuery(id+"F15.opExtrude","SWEPT_EDGE",EDGE,{"disambiguationData":[OSD([sQuery(id+"F5.wireOp",EDGE,"E138.bottom"),sQuery(id+"F5.wireOp",EDGE,"E153"),sQuery(id+"F5.wireOp",EDGE,"E176")])]});
            var Q2;
            Q2=makeQuery(id+"F15.opExtrude","SWEPT_EDGE",EDGE,{"disambiguationData":[OSD([sQuery(id+"F5.wireOp",EDGE,"E152"),sQuery(id+"F5.wireOp",EDGE,"E189")])]});
            fillet(context, id + "F16", {"entities" : qUnion([Q0, Q1, Q2]), "tangentPropagation" : true, "radius" : 127 * mm, "defaultsChanged" : true, "vertexSettings" : [], "allowEdgeOverflow" : false});
        }
        {
            var Q0;
            Q0=makeQuery(id+"F9.opExtrude","SWEPT_EDGE",EDGE,{"disambiguationData":[OSD([sQuery(id+"F8.wireOp",EDGE,"E305.left"),sQuery(id+"F8.wireOp",EDGE,"E307.top"),sQuery(id+"F8.wireOp",EDGE,"E307.left")])]});
            fillet(context, id + "F17", {"entities" : qUnion([Q0]), "tangentPropagation" : true, "radius" : 50.8 * mm, "defaultsChanged" : true, "vertexSettings" : [], "allowEdgeOverflow" : false});
        }
        {
            var Q0;
            Q0=makeQuery(id+"F9.opExtrude","SWEPT_EDGE",EDGE,{"disambiguationData":[OSD([sQuery(id+"F8.wireOp",EDGE,"E300"),sQuery(id+"F8.wireOp",EDGE,"E306")])]});
            fillet(context, id + "F18", {"entities" : qUnion([Q0]), "tangentPropagation" : true, "radius" : 12.7 * mm, "defaultsChanged" : true, "vertexSettings" : [], "allowEdgeOverflow" : false});
        }
        {
            var Q0;
            Q0=makeQuery(id+"F11.opExtrude","SWEPT_EDGE",EDGE,{"disambiguationData":[OSD([sQuery(id+"F8.wireOp",EDGE,"E305.left"),sQuery(id+"F8.wireOp",EDGE,"E307.top"),sQuery(id+"F8.wireOp",EDGE,"E307.left")])]});
            fillet(context, id + "F19", {"entities" : qUnion([Q0]), "tangentPropagation" : true, "radius" : 127 * mm, "defaultsChanged" : true, "vertexSettings" : [], "allowEdgeOverflow" : false});
        }
        {
            var Q0;
            Q0=makeQuery(id+"F6.opExtrude","SWEPT_EDGE",EDGE,{"disambiguationData":[OSD([sQuery(id+"F5.wireOp",EDGE,"E136.left"),sQuery(id+"F5.wireOp",EDGE,"E138.top"),sQuery(id+"F5.wireOp",EDGE,"E138.left")])]});
            fillet(context, id + "F20", {"entities" : qUnion([Q0]), "tangentPropagation" : true, "radius" : 127 * mm, "defaultsChanged" : true, "vertexSettings" : [], "allowEdgeOverflow" : false});
        }
        {
            var Q0;
            Q0=qCreatedBy(makeId("Top.planeOp"),FACE);
            var sketch = newSketch(context, id + "F21", { "sketchPlane" : qUnion([Q0])});
            skPoint(sketch, "E341.middle", {"position": v(0, 0) * mm});
            skCircle(sketch, "E342", {"center": v(0, 0) * mm, "radius": 3302 * mm, "construction": true});
            skCircle(sketch, "E343", {"center": v(0, 0) * mm, "radius": 3810 * mm});
            skCircle(sketch, "E344", {"center": v(0, 0) * mm, "radius": 3492.5 * mm, "construction": true});
            skCircle(sketch, "E345", {"center": v(0, 0) * mm, "radius": 4064 * mm});
            skLineSegment(sketch, "E346", {"start": v(0, 0) * mm, "end": v(-2873.68, 2873.68) * mm});
            skCircle(sketch, "E347", {"center": v(0, 0) * mm, "radius": 3683 * mm});
            skLineSegment(sketch, "E348", {"start": v(-3240.3, 635.33) * mm, "end": v(-3658.91, 1062.3) * mm});
            skLineSegment(sketch, "E349", {"start": v(-3683, 0) * mm, "end": v(-3683, 228.6) * mm});
            skLineSegment(sketch, "E350", {"start": v(-3683, 228.6) * mm, "end": v(-3273.6, 432.13) * mm});
            skLineSegment(sketch, "E351", {"start": v(0, 0) * mm, "end": v(-4064, 0) * mm});
            skLineSegment(sketch, "E352.0", {"start": v(-3273.6, 432.13) * mm, "end": v(-3240.3, 432.13) * mm, "construction": true});
            skLineSegment(sketch, "E352.1", {"start": v(-3240.3, 432.13) * mm, "end": v(-3240.3, 635.33) * mm, "construction": true});
            skLineSegment(sketch, "E353", {"start": v(-3683, 0) * mm, "end": v(-3683, -228.6) * mm});
            skLineSegment(sketch, "E354", {"start": v(-3683, -228.6) * mm, "end": v(-3273.6, -432.13) * mm});
            skLineSegment(sketch, "E355", {"start": v(0, 0) * mm, "end": v(-2873.68, -2873.68) * mm});
            skLineSegment(sketch, "E356", {"start": v(-3240.3, -635.33) * mm, "end": v(-3861, -1268.4) * mm});
            skLineSegment(sketch, "E357", {"start": v(-4010.78, 655.57) * mm, "end": v(0, 0) * mm, "construction": true});
            skLineSegment(sketch, "E358", {"start": v(-4010.78, -655.57) * mm, "end": v(0, 0) * mm, "construction": true});
            skCircle(sketch, "E359", {"center": v(-3359.02, 549.04) * mm, "radius": 50.8 * mm});
            skCircle(sketch, "E360", {"center": v(-3359.02, -549.04) * mm, "radius": 50.8 * mm});
            skCircle(sketch, "E361", {"center": v(-2872.23, 2692.63) * mm, "radius": 50.8 * mm});
            skCircle(sketch, "E362", {"center": v(-2872.23, -2692.63) * mm, "radius": 50.8 * mm});
            skLineSegment(sketch, "E363", {"start": v(-3273.6, -432.13) * mm, "end": v(-3240.3, -635.33) * mm});
            skArc(sketch, "E364", {"start": v(-3240.3, -635.33) * mm, "mid": v(-2914.23, -1552.57) * mm, "end": v(-2334.87, -2334.87) * mm});
            skLineSegment(sketch, "E365", {"start": v(-3240.3, 635.33) * mm, "end": v(-3273.6, 432.13) * mm});
            skSolve(sketch);
        }
        {
            var Q0;
            Q0=makeQuery(id+"F21.imprint","IMPRINT",FACE,{"disambiguationData":[TD([[makeQuery(id+"F21.imprint","IMPRINT",EDGE,{"derivedFrom":sQuery(id+"F21.wireOp",EDGE,"E361")}),-1.0]])]});
            var Q1;
            {var subQ7=sQuery(id+"F21.wireOp",EDGE,"E349");Q1=makeQuery(id+"F21.imprint","IMPRINT",FACE,{"disambiguationData":[TD([[makeQuery(id+"F21.imprint","IMPRINT",EDGE,{"derivedFrom":subQ7}),1.0]])]});}
            var Q2;
            Q2=makeQuery(id+"F21.imprint","IMPRINT",FACE,{"disambiguationData":[TD([[makeQuery(id+"F21.imprint","IMPRINT",EDGE,{"derivedFrom":sQuery(id+"F21.wireOp",EDGE,"E359")}),-1.0]])]});
            var Q3;
            {var subQ0=sQuery(id+"F21.wireOp",EDGE,"E351");var subQ1=sQuery(id+"F21.wireOp",EDGE,"E343");var subQ2=makeQuery(id+"F21.imprint","INTERSECT",VERTEX,{"derivedFrom":[subQ1,subQ0]});Q3=makeQuery(id+"F21.imprint","IMPRINT",FACE,{"disambiguationData":[TD([[makeQuery(id+"F21.imprint","IMPRINT",EDGE,{"disambiguationData":[TD([[subQ2,-1.0]])],"derivedFrom":subQ1}),-1.0]])]});}
            var Q4;
            {var subQ0=sQuery(id+"F21.wireOp",EDGE,"E353");Q4=makeQuery(id+"F21.imprint","IMPRINT",FACE,{"disambiguationData":[TD([[makeQuery(id+"F21.imprint","IMPRINT",EDGE,{"derivedFrom":subQ0}),-1.0]])]});}
            var Q5;
            Q5=makeQuery(id+"F21.imprint","IMPRINT",FACE,{"disambiguationData":[TD([[makeQuery(id+"F21.imprint","IMPRINT",EDGE,{"derivedFrom":sQuery(id+"F21.wireOp",EDGE,"E360")}),-1.0]])]});
            var Q6;
            {var subQ0=sQuery(id+"F21.wireOp",EDGE,"E356");var subQ1=sQuery(id+"F21.wireOp",EDGE,"E343");var subQ2=makeQuery(id+"F21.imprint","INTERSECT",VERTEX,{"derivedFrom":[subQ1,subQ0]});Q6=makeQuery(id+"F21.imprint","IMPRINT",FACE,{"disambiguationData":[TD([[makeQuery(id+"F21.imprint","IMPRINT",EDGE,{"disambiguationData":[TD([[subQ2,-1.0]])],"derivedFrom":subQ1}),1.0]])]});}
            var Q7;
            Q7=makeQuery(id+"F21.imprint","IMPRINT",FACE,{"disambiguationData":[TD([[makeQuery(id+"F21.imprint","IMPRINT",EDGE,{"derivedFrom":sQuery(id+"F21.wireOp",EDGE,"E362")}),-1.0]])]});
            var Q8;
            {var subQ5=sQuery(id+"F21.wireOp",EDGE,"E364");Q8=makeQuery(id+"F21.imprint","IMPRINT",FACE,{"disambiguationData":[TD([[makeQuery(id+"F21.imprint","IMPRINT",EDGE,{"derivedFrom":subQ5}),-1.0]])]});}
            extrude(context, id + "F22", {"entities" : qUnion([Q0, Q1, Q2, Q3, Q4, Q5, Q6, Q7, Q8]), "depth" : 152.4 * mm, "offsetDistance" : 25.4 * mm});
        }
        {
            var Q0;
            Q0=makeQuery(id+"F22.opExtrude","SWEPT_EDGE",EDGE,{"disambiguationData":[OSD([sQuery(id+"F21.wireOp",EDGE,"E343"),sQuery(id+"F21.wireOp",EDGE,"E346")])]});
            var Q1;
            Q1=makeQuery(id+"F22.opExtrude","SWEPT_EDGE",EDGE,{"disambiguationData":[OSD([sQuery(id+"F21.wireOp",EDGE,"E345"),sQuery(id+"F21.wireOp",EDGE,"E346")])]});
            var Q2;
            Q2=makeQuery(id+"F22.opExtrude","SWEPT_EDGE",EDGE,{"disambiguationData":[OSD([sQuery(id+"F21.wireOp",EDGE,"E348"),sQuery(id+"F21.wireOp",EDGE,"E365")])]});
            var Q3;
            Q3=makeQuery(id+"F22.opExtrude","SWEPT_EDGE",EDGE,{"disambiguationData":[OSD([sQuery(id+"F21.wireOp",EDGE,"E350"),sQuery(id+"F21.wireOp",EDGE,"E365")])]});
            var Q4;
            Q4=makeQuery(id+"F22.opExtrude","SWEPT_EDGE",EDGE,{"disambiguationData":[OSD([sQuery(id+"F21.wireOp",EDGE,"E349"),sQuery(id+"F21.wireOp",EDGE,"E350")])]});
            var Q5;
            Q5=makeQuery(id+"F22.opExtrude","SWEPT_EDGE",EDGE,{"disambiguationData":[OSD([sQuery(id+"F21.wireOp",EDGE,"E353"),sQuery(id+"F21.wireOp",EDGE,"E354")])]});
            var Q6;
            Q6=makeQuery(id+"F22.opExtrude","SWEPT_EDGE",EDGE,{"disambiguationData":[OSD([sQuery(id+"F21.wireOp",EDGE,"E354"),sQuery(id+"F21.wireOp",EDGE,"E363")])]});
            var Q7;
            Q7=makeQuery(id+"F22.opExtrude","SWEPT_EDGE",EDGE,{"disambiguationData":[OSD([sQuery(id+"F21.wireOp",EDGE,"E345"),sQuery(id+"F21.wireOp",EDGE,"E355")])]});
            fillet(context, id + "F23", {"entities" : qUnion([Q0, Q1, Q2, Q3, Q4, Q5, Q6, Q7]), "tangentPropagation" : true, "radius" : 127 * mm, "defaultsChanged" : false, "vertexSettings" : [], "allowEdgeOverflow" : false});
        }
        {
            var Q0;
            Q0=makeQuery(id+"F22.opExtrude","SWEPT_EDGE",EDGE,{"disambiguationData":[OSD([sQuery(id+"F21.wireOp",EDGE,"E343"),sQuery(id+"F21.wireOp",EDGE,"E348")])]});
            fillet(context, id + "F24", {"entities" : qUnion([Q0]), "tangentPropagation" : true, "radius" : 2032 * mm, "defaultsChanged" : true, "vertexSettings" : [], "allowEdgeOverflow" : false});
        }
        {
            var Q0;
            Q0=makeQuery(id+"F22.opExtrude","SWEPT_EDGE",EDGE,{"disambiguationData":[OSD([sQuery(id+"F21.wireOp",EDGE,"E355"),sQuery(id+"F21.wireOp",EDGE,"E364")])]});
            chamfer(context, id + "F25", {"entities" : qUnion([Q0]), "chamferType" : ChamferType.TWO_OFFSETS, "width1" : 558.8 * mm, "oppositeDirection" : false, "width2" : 635 * mm, "tangentPropagation" : true});
        }
        {
            var Q0;
            Q0=makeQuery(id+"F21.imprint","IMPRINT",FACE,{"disambiguationData":[TD([[makeQuery(id+"F21.imprint","IMPRINT",EDGE,{"derivedFrom":sQuery(id+"F21.wireOp",EDGE,"Vg3eGnU8-vRcV-Nsrl-cUM7-ReKbhwyZX7Up")}),1.0]])]});
            var Q1;
            Q1=makeQuery(id+"F21.imprint","IMPRINT",FACE,{"disambiguationData":[TD([[makeQuery(id+"F21.imprint","IMPRINT",EDGE,{"derivedFrom":sQuery(id+"F21.wireOp",EDGE,"E360")}),1.0]])]});
            extrude(context, id + "F26", {"entities" : qUnion([Q0, Q1]), "operationType" : NewBodyOperationType.REMOVE, "depth" : 152.4 * mm, "offsetDistance" : 25.4 * mm});
        }
    });
